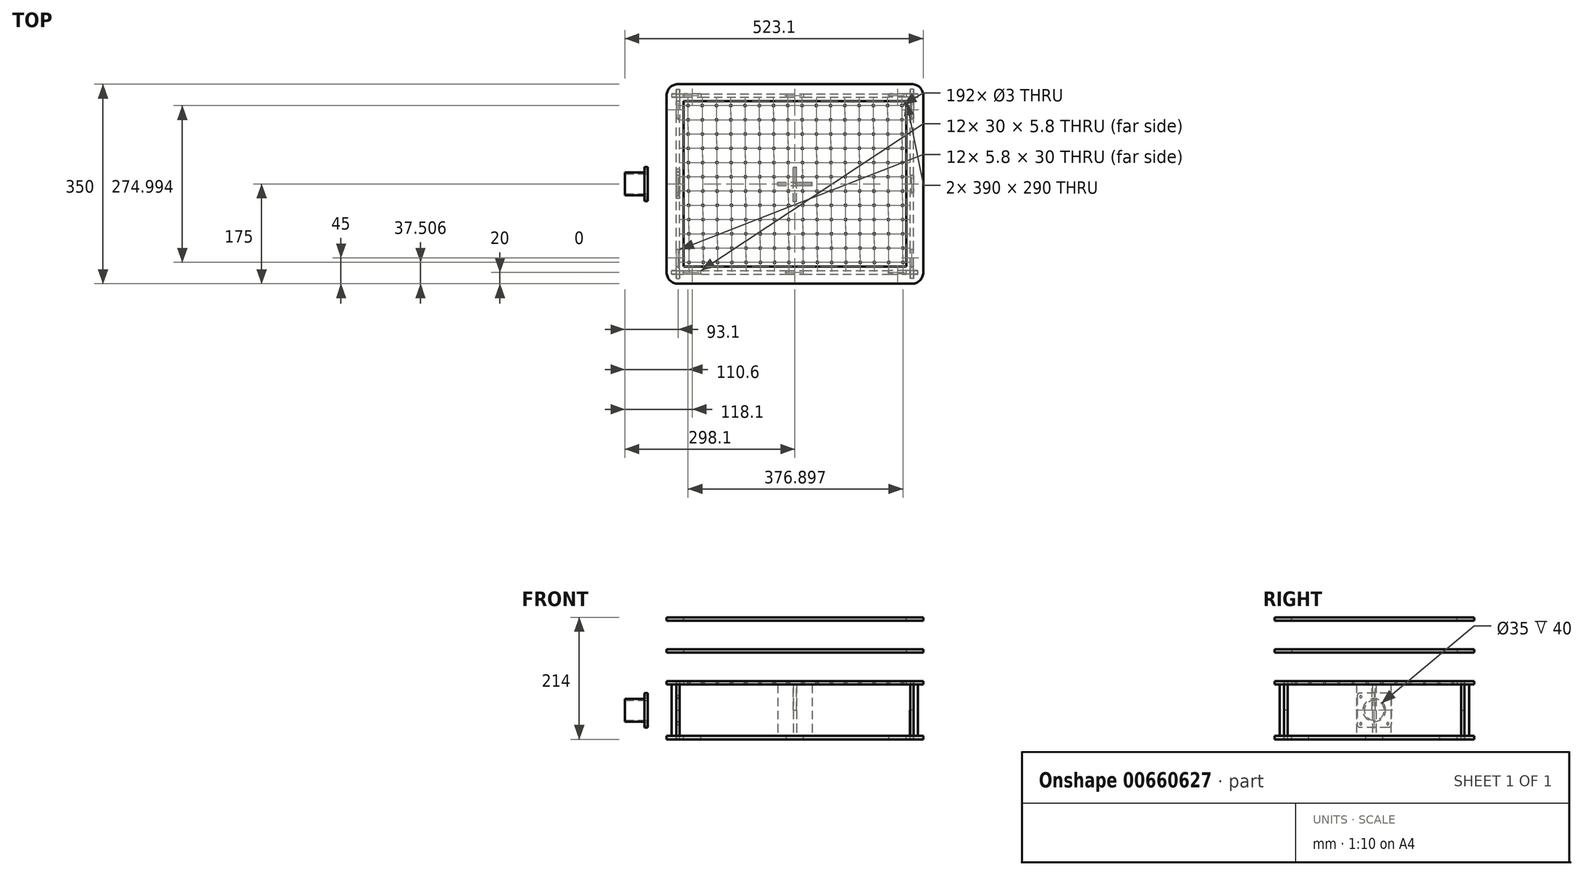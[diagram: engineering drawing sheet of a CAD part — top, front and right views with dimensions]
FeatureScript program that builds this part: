
annotation { "Feature Type Name" : "Feature", "Feature Type Description" : "" }
export const myFeature = defineFeature(function(context is Context, id is Id, definition is map)
    precondition{}
    {
        {
            var Q0;
            Q0=qCreatedBy(makeId("Top.planeOp"),FACE);
            var sketch = newSketch(context, id + "F0", { "sketchPlane" : qUnion([Q0])});
            skLineSegment(sketch, "E0.bottom", {"start": v(205, 175) * mm, "end": v(-205, 175) * mm});
            skLineSegment(sketch, "E0.top", {"start": v(205, -175) * mm, "end": v(-205, -175) * mm});
            skLineSegment(sketch, "E0.left", {"start": v(225, 155) * mm, "end": v(225, -155) * mm});
            skLineSegment(sketch, "E0.right", {"start": v(-225, 155) * mm, "end": v(-225, -155) * mm});
            skPoint(sketch, "E0.middle", {"position": v(0, 0) * mm});
            skPoint(sketch, "E1.visualSharp", {"position": v(-225, 175) * mm});
            skArc(sketch, "E1.filletArc", {"start": v(-205, 175) * mm, "mid": v(-219.14, 169.14) * mm, "end": v(-225, 155) * mm});
            skPoint(sketch, "E2.visualSharp", {"position": v(225, 175) * mm});
            skArc(sketch, "E2.filletArc", {"start": v(225, 155) * mm, "mid": v(219.14, 169.14) * mm, "end": v(205, 175) * mm});
            skPoint(sketch, "E3.visualSharp", {"position": v(225, -175) * mm});
            skArc(sketch, "E3.filletArc", {"start": v(205, -175) * mm, "mid": v(219.14, -169.14) * mm, "end": v(225, -155) * mm});
            skPoint(sketch, "E4.visualSharp", {"position": v(-225, -175) * mm});
            skArc(sketch, "E4.filletArc", {"start": v(-225, -155) * mm, "mid": v(-219.14, -169.14) * mm, "end": v(-205, -175) * mm});
            skLineSegment(sketch, "E5", {"start": v(205, -155) * mm, "end": v(205, 155) * mm, "construction": true});
            skLineSegment(sketch, "E6.bottom", {"start": v(-205, 155) * mm, "end": v(205, 155) * mm, "construction": true});
            skLineSegment(sketch, "E6.top", {"start": v(-205, -155) * mm, "end": v(205, -155) * mm, "construction": true});
            skLineSegment(sketch, "E6.left", {"start": v(-205, 155) * mm, "end": v(-205, -155) * mm, "construction": true});
            skCircle(sketch, "E7", {"center": v(-187.5, 137.5) * mm, "radius": 1.5 * mm});
            skCircle(sketch, "E8.1.0.0", {"center": v(-162.5, 137.5) * mm, "radius": 1.5 * mm});
            skCircle(sketch, "E8.2.0.0", {"center": v(-137.5, 137.5) * mm, "radius": 1.5 * mm});
            skCircle(sketch, "E8.3.0.0", {"center": v(-112.5, 137.5) * mm, "radius": 1.5 * mm});
            skCircle(sketch, "E8.4.0.0", {"center": v(-87.5, 137.5) * mm, "radius": 1.5 * mm});
            skCircle(sketch, "E8.5.0.0", {"center": v(-62.5, 137.5) * mm, "radius": 1.5 * mm});
            skCircle(sketch, "E8.6.0.0", {"center": v(-37.5, 137.5) * mm, "radius": 1.5 * mm});
            skCircle(sketch, "E8.7.0.0", {"center": v(-12.5, 137.5) * mm, "radius": 1.5 * mm});
            skCircle(sketch, "E8.8.0.0", {"center": v(12.5, 137.5) * mm, "radius": 1.5 * mm});
            skCircle(sketch, "E8.9.0.0", {"center": v(37.5, 137.5) * mm, "radius": 1.5 * mm});
            skCircle(sketch, "E8.10.0.0", {"center": v(62.5, 137.5) * mm, "radius": 1.5 * mm});
            skCircle(sketch, "E8.11.0.0", {"center": v(87.5, 137.5) * mm, "radius": 1.5 * mm});
            skCircle(sketch, "E8.12.0.0", {"center": v(112.5, 137.5) * mm, "radius": 1.5 * mm});
            skCircle(sketch, "E8.13.0.0", {"center": v(137.5, 137.5) * mm, "radius": 1.5 * mm});
            skCircle(sketch, "E8.14.0.0", {"center": v(162.5, 137.5) * mm, "radius": 1.5 * mm});
            skLineSegment(sketch, "E8.direction1", {"start": v(-187.5, 137.5) * mm, "end": v(-162.5, 137.5) * mm, "construction": true});
            skCircle(sketch, "E9.1.0.0", {"center": v(-187.33, 112.5) * mm, "radius": 1.5 * mm});
            skCircle(sketch, "E9.2.0.0", {"center": v(-187.16, 87.5) * mm, "radius": 1.5 * mm});
            skCircle(sketch, "E9.3.0.0", {"center": v(-186.98, 62.5) * mm, "radius": 1.5 * mm});
            skCircle(sketch, "E9.4.0.0", {"center": v(-186.81, 37.5) * mm, "radius": 1.5 * mm});
            skCircle(sketch, "E9.5.0.0", {"center": v(-186.64, 12.5) * mm, "radius": 1.5 * mm});
            skCircle(sketch, "E9.6.0.0", {"center": v(-186.47, -12.5) * mm, "radius": 1.5 * mm});
            skCircle(sketch, "E9.7.0.0", {"center": v(-186.3, -37.5) * mm, "radius": 1.5 * mm});
            skCircle(sketch, "E9.8.0.0", {"center": v(-186.12, -62.5) * mm, "radius": 1.5 * mm});
            skCircle(sketch, "E9.9.0.0", {"center": v(-185.95, -87.5) * mm, "radius": 1.5 * mm});
            skCircle(sketch, "E9.10.0.0", {"center": v(-185.78, -112.5) * mm, "radius": 1.5 * mm});
            skCircle(sketch, "E9.11.0.0", {"center": v(-185.6, -137.5) * mm, "radius": 1.5 * mm});
            skLineSegment(sketch, "E9.direction1", {"start": v(-187.5, 137.5) * mm, "end": v(-187.33, 112.5) * mm, "construction": true});
            skCircle(sketch, "E10.0.15.0", {"center": v(187.5, 137.5) * mm, "radius": 1.5 * mm});
            skCircle(sketch, "E11.1.0.0", {"center": v(-162.33, 112.5) * mm, "radius": 1.5 * mm});
            skCircle(sketch, "E11.1.0.1", {"center": v(-162.16, 87.5) * mm, "radius": 1.5 * mm});
            skCircle(sketch, "E11.1.0.2", {"center": v(-161.98, 62.5) * mm, "radius": 1.5 * mm});
            skCircle(sketch, "E11.1.0.3", {"center": v(-161.81, 37.5) * mm, "radius": 1.5 * mm});
            skCircle(sketch, "E11.1.0.4", {"center": v(-161.64, 12.5) * mm, "radius": 1.5 * mm});
            skCircle(sketch, "E11.1.0.5", {"center": v(-161.47, -12.5) * mm, "radius": 1.5 * mm});
            skCircle(sketch, "E11.1.0.6", {"center": v(-161.3, -37.5) * mm, "radius": 1.5 * mm});
            skCircle(sketch, "E11.1.0.7", {"center": v(-161.12, -62.5) * mm, "radius": 1.5 * mm});
            skCircle(sketch, "E11.1.0.8", {"center": v(-160.95, -87.5) * mm, "radius": 1.5 * mm});
            skCircle(sketch, "E11.1.0.9", {"center": v(-160.78, -112.5) * mm, "radius": 1.5 * mm});
            skCircle(sketch, "E11.1.0.10", {"center": v(-160.6, -137.5) * mm, "radius": 1.5 * mm});
            skCircle(sketch, "E11.2.0.0", {"center": v(-137.33, 112.5) * mm, "radius": 1.5 * mm});
            skCircle(sketch, "E11.2.0.1", {"center": v(-137.16, 87.5) * mm, "radius": 1.5 * mm});
            skCircle(sketch, "E11.2.0.2", {"center": v(-136.98, 62.5) * mm, "radius": 1.5 * mm});
            skCircle(sketch, "E11.2.0.3", {"center": v(-136.81, 37.5) * mm, "radius": 1.5 * mm});
            skCircle(sketch, "E11.2.0.4", {"center": v(-136.64, 12.5) * mm, "radius": 1.5 * mm});
            skCircle(sketch, "E11.2.0.5", {"center": v(-136.47, -12.5) * mm, "radius": 1.5 * mm});
            skCircle(sketch, "E11.2.0.6", {"center": v(-136.3, -37.5) * mm, "radius": 1.5 * mm});
            skCircle(sketch, "E11.2.0.7", {"center": v(-136.12, -62.5) * mm, "radius": 1.5 * mm});
            skCircle(sketch, "E11.2.0.8", {"center": v(-135.95, -87.5) * mm, "radius": 1.5 * mm});
            skCircle(sketch, "E11.2.0.9", {"center": v(-135.78, -112.5) * mm, "radius": 1.5 * mm});
            skCircle(sketch, "E11.2.0.10", {"center": v(-135.6, -137.5) * mm, "radius": 1.5 * mm});
            skCircle(sketch, "E11.3.0.0", {"center": v(-112.33, 112.5) * mm, "radius": 1.5 * mm});
            skCircle(sketch, "E11.3.0.1", {"center": v(-112.16, 87.5) * mm, "radius": 1.5 * mm});
            skCircle(sketch, "E11.3.0.2", {"center": v(-111.98, 62.5) * mm, "radius": 1.5 * mm});
            skCircle(sketch, "E11.3.0.3", {"center": v(-111.81, 37.5) * mm, "radius": 1.5 * mm});
            skCircle(sketch, "E11.3.0.4", {"center": v(-111.64, 12.5) * mm, "radius": 1.5 * mm});
            skCircle(sketch, "E11.3.0.5", {"center": v(-111.47, -12.5) * mm, "radius": 1.5 * mm});
            skCircle(sketch, "E11.3.0.6", {"center": v(-111.3, -37.5) * mm, "radius": 1.5 * mm});
            skCircle(sketch, "E11.3.0.7", {"center": v(-111.12, -62.5) * mm, "radius": 1.5 * mm});
            skCircle(sketch, "E11.3.0.8", {"center": v(-110.95, -87.5) * mm, "radius": 1.5 * mm});
            skCircle(sketch, "E11.3.0.9", {"center": v(-110.78, -112.5) * mm, "radius": 1.5 * mm});
            skCircle(sketch, "E11.3.0.10", {"center": v(-110.6, -137.5) * mm, "radius": 1.5 * mm});
            skCircle(sketch, "E11.4.0.0", {"center": v(-87.33, 112.5) * mm, "radius": 1.5 * mm});
            skCircle(sketch, "E11.4.0.1", {"center": v(-87.16, 87.5) * mm, "radius": 1.5 * mm});
            skCircle(sketch, "E11.4.0.2", {"center": v(-86.98, 62.5) * mm, "radius": 1.5 * mm});
            skCircle(sketch, "E11.4.0.3", {"center": v(-86.81, 37.5) * mm, "radius": 1.5 * mm});
            skCircle(sketch, "E11.4.0.4", {"center": v(-86.64, 12.5) * mm, "radius": 1.5 * mm});
            skCircle(sketch, "E11.4.0.5", {"center": v(-86.47, -12.5) * mm, "radius": 1.5 * mm});
            skCircle(sketch, "E11.4.0.6", {"center": v(-86.3, -37.5) * mm, "radius": 1.5 * mm});
            skCircle(sketch, "E11.4.0.7", {"center": v(-86.12, -62.5) * mm, "radius": 1.5 * mm});
            skCircle(sketch, "E11.4.0.8", {"center": v(-85.95, -87.5) * mm, "radius": 1.5 * mm});
            skCircle(sketch, "E11.4.0.9", {"center": v(-85.78, -112.5) * mm, "radius": 1.5 * mm});
            skCircle(sketch, "E11.4.0.10", {"center": v(-85.6, -137.5) * mm, "radius": 1.5 * mm});
            skCircle(sketch, "E11.5.0.0", {"center": v(-62.33, 112.5) * mm, "radius": 1.5 * mm});
            skCircle(sketch, "E11.5.0.1", {"center": v(-62.16, 87.5) * mm, "radius": 1.5 * mm});
            skCircle(sketch, "E11.5.0.2", {"center": v(-61.98, 62.5) * mm, "radius": 1.5 * mm});
            skCircle(sketch, "E11.5.0.3", {"center": v(-61.81, 37.5) * mm, "radius": 1.5 * mm});
            skCircle(sketch, "E11.5.0.4", {"center": v(-61.64, 12.5) * mm, "radius": 1.5 * mm});
            skCircle(sketch, "E11.5.0.5", {"center": v(-61.47, -12.5) * mm, "radius": 1.5 * mm});
            skCircle(sketch, "E11.5.0.6", {"center": v(-61.3, -37.5) * mm, "radius": 1.5 * mm});
            skCircle(sketch, "E11.5.0.7", {"center": v(-61.12, -62.5) * mm, "radius": 1.5 * mm});
            skCircle(sketch, "E11.5.0.8", {"center": v(-60.95, -87.5) * mm, "radius": 1.5 * mm});
            skCircle(sketch, "E11.5.0.9", {"center": v(-60.78, -112.5) * mm, "radius": 1.5 * mm});
            skCircle(sketch, "E11.5.0.10", {"center": v(-60.6, -137.5) * mm, "radius": 1.5 * mm});
            skCircle(sketch, "E11.6.0.0", {"center": v(-37.33, 112.5) * mm, "radius": 1.5 * mm});
            skCircle(sketch, "E11.6.0.1", {"center": v(-37.16, 87.5) * mm, "radius": 1.5 * mm});
            skCircle(sketch, "E11.6.0.2", {"center": v(-36.98, 62.5) * mm, "radius": 1.5 * mm});
            skCircle(sketch, "E11.6.0.3", {"center": v(-36.81, 37.5) * mm, "radius": 1.5 * mm});
            skCircle(sketch, "E11.6.0.4", {"center": v(-36.64, 12.5) * mm, "radius": 1.5 * mm});
            skCircle(sketch, "E11.6.0.5", {"center": v(-36.47, -12.5) * mm, "radius": 1.5 * mm});
            skCircle(sketch, "E11.6.0.6", {"center": v(-36.3, -37.5) * mm, "radius": 1.5 * mm});
            skCircle(sketch, "E11.6.0.7", {"center": v(-36.12, -62.5) * mm, "radius": 1.5 * mm});
            skCircle(sketch, "E11.6.0.8", {"center": v(-35.95, -87.5) * mm, "radius": 1.5 * mm});
            skCircle(sketch, "E11.6.0.9", {"center": v(-35.78, -112.5) * mm, "radius": 1.5 * mm});
            skCircle(sketch, "E11.6.0.10", {"center": v(-35.6, -137.5) * mm, "radius": 1.5 * mm});
            skCircle(sketch, "E11.7.0.0", {"center": v(-12.33, 112.5) * mm, "radius": 1.5 * mm});
            skCircle(sketch, "E11.7.0.1", {"center": v(-12.16, 87.5) * mm, "radius": 1.5 * mm});
            skCircle(sketch, "E11.7.0.2", {"center": v(-11.98, 62.5) * mm, "radius": 1.5 * mm});
            skCircle(sketch, "E11.7.0.3", {"center": v(-11.81, 37.5) * mm, "radius": 1.5 * mm});
            skCircle(sketch, "E11.7.0.4", {"center": v(-11.64, 12.5) * mm, "radius": 1.5 * mm});
            skCircle(sketch, "E11.7.0.5", {"center": v(-11.47, -12.5) * mm, "radius": 1.5 * mm});
            skCircle(sketch, "E11.7.0.6", {"center": v(-11.3, -37.5) * mm, "radius": 1.5 * mm});
            skCircle(sketch, "E11.7.0.7", {"center": v(-11.12, -62.5) * mm, "radius": 1.5 * mm});
            skCircle(sketch, "E11.7.0.8", {"center": v(-10.95, -87.5) * mm, "radius": 1.5 * mm});
            skCircle(sketch, "E11.7.0.9", {"center": v(-10.78, -112.5) * mm, "radius": 1.5 * mm});
            skCircle(sketch, "E11.7.0.10", {"center": v(-10.6, -137.5) * mm, "radius": 1.5 * mm});
            skCircle(sketch, "E11.8.0.0", {"center": v(12.67, 112.5) * mm, "radius": 1.5 * mm});
            skCircle(sketch, "E11.8.0.1", {"center": v(12.84, 87.5) * mm, "radius": 1.5 * mm});
            skCircle(sketch, "E11.8.0.2", {"center": v(13.02, 62.5) * mm, "radius": 1.5 * mm});
            skCircle(sketch, "E11.8.0.3", {"center": v(13.19, 37.5) * mm, "radius": 1.5 * mm});
            skCircle(sketch, "E11.8.0.4", {"center": v(13.36, 12.5) * mm, "radius": 1.5 * mm});
            skCircle(sketch, "E11.8.0.5", {"center": v(13.53, -12.5) * mm, "radius": 1.5 * mm});
            skCircle(sketch, "E11.8.0.6", {"center": v(13.7, -37.5) * mm, "radius": 1.5 * mm});
            skCircle(sketch, "E11.8.0.7", {"center": v(13.88, -62.5) * mm, "radius": 1.5 * mm});
            skCircle(sketch, "E11.8.0.8", {"center": v(14.05, -87.5) * mm, "radius": 1.5 * mm});
            skCircle(sketch, "E11.8.0.9", {"center": v(14.22, -112.5) * mm, "radius": 1.5 * mm});
            skCircle(sketch, "E11.8.0.10", {"center": v(14.4, -137.5) * mm, "radius": 1.5 * mm});
            skCircle(sketch, "E11.9.0.0", {"center": v(37.67, 112.5) * mm, "radius": 1.5 * mm});
            skCircle(sketch, "E11.9.0.1", {"center": v(37.84, 87.5) * mm, "radius": 1.5 * mm});
            skCircle(sketch, "E11.9.0.2", {"center": v(38.02, 62.5) * mm, "radius": 1.5 * mm});
            skCircle(sketch, "E11.9.0.3", {"center": v(38.19, 37.5) * mm, "radius": 1.5 * mm});
            skCircle(sketch, "E11.9.0.4", {"center": v(38.36, 12.5) * mm, "radius": 1.5 * mm});
            skCircle(sketch, "E11.9.0.5", {"center": v(38.53, -12.5) * mm, "radius": 1.5 * mm});
            skCircle(sketch, "E11.9.0.6", {"center": v(38.7, -37.5) * mm, "radius": 1.5 * mm});
            skCircle(sketch, "E11.9.0.7", {"center": v(38.88, -62.5) * mm, "radius": 1.5 * mm});
            skCircle(sketch, "E11.9.0.8", {"center": v(39.05, -87.5) * mm, "radius": 1.5 * mm});
            skCircle(sketch, "E11.9.0.9", {"center": v(39.22, -112.5) * mm, "radius": 1.5 * mm});
            skCircle(sketch, "E11.9.0.10", {"center": v(39.4, -137.5) * mm, "radius": 1.5 * mm});
            skCircle(sketch, "E11.10.0.0", {"center": v(62.67, 112.5) * mm, "radius": 1.5 * mm});
            skCircle(sketch, "E11.10.0.1", {"center": v(62.84, 87.5) * mm, "radius": 1.5 * mm});
            skCircle(sketch, "E11.10.0.2", {"center": v(63.02, 62.5) * mm, "radius": 1.5 * mm});
            skCircle(sketch, "E11.10.0.3", {"center": v(63.19, 37.5) * mm, "radius": 1.5 * mm});
            skCircle(sketch, "E11.10.0.4", {"center": v(63.36, 12.5) * mm, "radius": 1.5 * mm});
            skCircle(sketch, "E11.10.0.5", {"center": v(63.53, -12.5) * mm, "radius": 1.5 * mm});
            skCircle(sketch, "E11.10.0.6", {"center": v(63.7, -37.5) * mm, "radius": 1.5 * mm});
            skCircle(sketch, "E11.10.0.7", {"center": v(63.88, -62.5) * mm, "radius": 1.5 * mm});
            skCircle(sketch, "E11.10.0.8", {"center": v(64.05, -87.5) * mm, "radius": 1.5 * mm});
            skCircle(sketch, "E11.10.0.9", {"center": v(64.22, -112.5) * mm, "radius": 1.5 * mm});
            skCircle(sketch, "E11.10.0.10", {"center": v(64.4, -137.5) * mm, "radius": 1.5 * mm});
            skCircle(sketch, "E11.11.0.0", {"center": v(87.67, 112.5) * mm, "radius": 1.5 * mm});
            skCircle(sketch, "E11.11.0.1", {"center": v(87.84, 87.5) * mm, "radius": 1.5 * mm});
            skCircle(sketch, "E11.11.0.2", {"center": v(88.02, 62.5) * mm, "radius": 1.5 * mm});
            skCircle(sketch, "E11.11.0.3", {"center": v(88.19, 37.5) * mm, "radius": 1.5 * mm});
            skCircle(sketch, "E11.11.0.4", {"center": v(88.36, 12.5) * mm, "radius": 1.5 * mm});
            skCircle(sketch, "E11.11.0.5", {"center": v(88.53, -12.5) * mm, "radius": 1.5 * mm});
            skCircle(sketch, "E11.11.0.6", {"center": v(88.7, -37.5) * mm, "radius": 1.5 * mm});
            skCircle(sketch, "E11.11.0.7", {"center": v(88.88, -62.5) * mm, "radius": 1.5 * mm});
            skCircle(sketch, "E11.11.0.8", {"center": v(89.05, -87.5) * mm, "radius": 1.5 * mm});
            skCircle(sketch, "E11.11.0.9", {"center": v(89.22, -112.5) * mm, "radius": 1.5 * mm});
            skCircle(sketch, "E11.11.0.10", {"center": v(89.4, -137.5) * mm, "radius": 1.5 * mm});
            skCircle(sketch, "E11.12.0.0", {"center": v(112.67, 112.5) * mm, "radius": 1.5 * mm});
            skCircle(sketch, "E11.12.0.1", {"center": v(112.84, 87.5) * mm, "radius": 1.5 * mm});
            skCircle(sketch, "E11.12.0.2", {"center": v(113.02, 62.5) * mm, "radius": 1.5 * mm});
            skCircle(sketch, "E11.12.0.3", {"center": v(113.19, 37.5) * mm, "radius": 1.5 * mm});
            skCircle(sketch, "E11.12.0.4", {"center": v(113.36, 12.5) * mm, "radius": 1.5 * mm});
            skCircle(sketch, "E11.12.0.5", {"center": v(113.53, -12.5) * mm, "radius": 1.5 * mm});
            skCircle(sketch, "E11.12.0.6", {"center": v(113.7, -37.5) * mm, "radius": 1.5 * mm});
            skCircle(sketch, "E11.12.0.7", {"center": v(113.88, -62.5) * mm, "radius": 1.5 * mm});
            skCircle(sketch, "E11.12.0.8", {"center": v(114.05, -87.5) * mm, "radius": 1.5 * mm});
            skCircle(sketch, "E11.12.0.9", {"center": v(114.22, -112.5) * mm, "radius": 1.5 * mm});
            skCircle(sketch, "E11.12.0.10", {"center": v(114.4, -137.5) * mm, "radius": 1.5 * mm});
            skCircle(sketch, "E11.13.0.0", {"center": v(137.67, 112.5) * mm, "radius": 1.5 * mm});
            skCircle(sketch, "E11.13.0.1", {"center": v(137.84, 87.5) * mm, "radius": 1.5 * mm});
            skCircle(sketch, "E11.13.0.2", {"center": v(138.02, 62.5) * mm, "radius": 1.5 * mm});
            skCircle(sketch, "E11.13.0.3", {"center": v(138.19, 37.5) * mm, "radius": 1.5 * mm});
            skCircle(sketch, "E11.13.0.4", {"center": v(138.36, 12.5) * mm, "radius": 1.5 * mm});
            skCircle(sketch, "E11.13.0.5", {"center": v(138.53, -12.5) * mm, "radius": 1.5 * mm});
            skCircle(sketch, "E11.13.0.6", {"center": v(138.7, -37.5) * mm, "radius": 1.5 * mm});
            skCircle(sketch, "E11.13.0.7", {"center": v(138.88, -62.5) * mm, "radius": 1.5 * mm});
            skCircle(sketch, "E11.13.0.8", {"center": v(139.05, -87.5) * mm, "radius": 1.5 * mm});
            skCircle(sketch, "E11.13.0.9", {"center": v(139.22, -112.5) * mm, "radius": 1.5 * mm});
            skCircle(sketch, "E11.13.0.10", {"center": v(139.4, -137.5) * mm, "radius": 1.5 * mm});
            skCircle(sketch, "E11.14.0.0", {"center": v(162.67, 112.5) * mm, "radius": 1.5 * mm});
            skCircle(sketch, "E11.14.0.1", {"center": v(162.84, 87.5) * mm, "radius": 1.5 * mm});
            skCircle(sketch, "E11.14.0.2", {"center": v(163.02, 62.5) * mm, "radius": 1.5 * mm});
            skCircle(sketch, "E11.14.0.3", {"center": v(163.19, 37.5) * mm, "radius": 1.5 * mm});
            skCircle(sketch, "E11.14.0.4", {"center": v(163.36, 12.5) * mm, "radius": 1.5 * mm});
            skCircle(sketch, "E11.14.0.5", {"center": v(163.53, -12.5) * mm, "radius": 1.5 * mm});
            skCircle(sketch, "E11.14.0.6", {"center": v(163.7, -37.5) * mm, "radius": 1.5 * mm});
            skCircle(sketch, "E11.14.0.7", {"center": v(163.88, -62.5) * mm, "radius": 1.5 * mm});
            skCircle(sketch, "E11.14.0.8", {"center": v(164.05, -87.5) * mm, "radius": 1.5 * mm});
            skCircle(sketch, "E11.14.0.9", {"center": v(164.22, -112.5) * mm, "radius": 1.5 * mm});
            skCircle(sketch, "E11.14.0.10", {"center": v(164.4, -137.5) * mm, "radius": 1.5 * mm});
            skCircle(sketch, "E11.15.0.0", {"center": v(187.67, 112.5) * mm, "radius": 1.5 * mm});
            skCircle(sketch, "E11.15.0.1", {"center": v(187.84, 87.5) * mm, "radius": 1.5 * mm});
            skCircle(sketch, "E11.15.0.2", {"center": v(188.02, 62.5) * mm, "radius": 1.5 * mm});
            skCircle(sketch, "E11.15.0.3", {"center": v(188.19, 37.5) * mm, "radius": 1.5 * mm});
            skCircle(sketch, "E11.15.0.4", {"center": v(188.36, 12.5) * mm, "radius": 1.5 * mm});
            skCircle(sketch, "E11.15.0.5", {"center": v(188.53, -12.5) * mm, "radius": 1.5 * mm});
            skCircle(sketch, "E11.15.0.6", {"center": v(188.7, -37.5) * mm, "radius": 1.5 * mm});
            skCircle(sketch, "E11.15.0.7", {"center": v(188.88, -62.5) * mm, "radius": 1.5 * mm});
            skCircle(sketch, "E11.15.0.8", {"center": v(189.05, -87.5) * mm, "radius": 1.5 * mm});
            skCircle(sketch, "E11.15.0.9", {"center": v(189.22, -112.5) * mm, "radius": 1.5 * mm});
            skCircle(sketch, "E11.15.0.10", {"center": v(189.4, -137.5) * mm, "radius": 1.5 * mm});
            skLineSegment(sketch, "E11.direction1", {"start": v(-187.33, 112.5) * mm, "end": v(-162.33, 112.5) * mm, "construction": true});
            skLineSegment(sketch, "E12", {"start": v(0, 0) * mm, "end": v(0, 209.09) * mm, "construction": true});
            skPoint(sketch, "E12.endSnap0", {"position": v(0, 175) * mm});
            skLineSegment(sketch, "E13", {"start": v(0, 209.09) * mm, "end": v(0, 128.36) * mm, "construction": true});
            skLineSegment(sketch, "E14", {"start": v(0, 0) * mm, "end": v(-306.75, 0) * mm, "construction": true});
            skLineSegment(sketch, "E15.bottom", {"start": v(-195, 157.9) * mm, "end": v(-165, 157.9) * mm});
            skLineSegment(sketch, "E15.top", {"start": v(-195, 152.1) * mm, "end": v(-165, 152.1) * mm});
            skLineSegment(sketch, "E15.left", {"start": v(-195, 157.9) * mm, "end": v(-195, 152.1) * mm});
            skLineSegment(sketch, "E15.right", {"start": v(-165, 157.9) * mm, "end": v(-165, 152.1) * mm});
            skLineSegment(sketch, "E16.bottom", {"start": v(-15, 157.9) * mm, "end": v(15, 157.9) * mm});
            skLineSegment(sketch, "E16.top", {"start": v(-15, 152.1) * mm, "end": v(15, 152.1) * mm});
            skLineSegment(sketch, "E16.left", {"start": v(-15, 157.9) * mm, "end": v(-15, 152.1) * mm});
            skLineSegment(sketch, "E16.right", {"start": v(15, 157.9) * mm, "end": v(15, 152.1) * mm});
            skLineSegment(sketch, "E17.MirrorCS", {"start": v(195, 157.9) * mm, "end": v(195, 152.1) * mm});
            skLineSegment(sketch, "E18.MirrorCS", {"start": v(195, 157.9) * mm, "end": v(165, 157.9) * mm});
            skLineSegment(sketch, "E19.MirrorCS", {"start": v(195, 152.1) * mm, "end": v(165, 152.1) * mm});
            skLineSegment(sketch, "E20.MirrorCS", {"start": v(165, 157.9) * mm, "end": v(165, 152.1) * mm});
            skLineSegment(sketch, "E21.MirrorCS", {"start": v(165, -157.9) * mm, "end": v(165, -152.1) * mm});
            skLineSegment(sketch, "E22.MirrorCS", {"start": v(195, -157.9) * mm, "end": v(165, -157.9) * mm});
            skLineSegment(sketch, "E23.MirrorCS", {"start": v(195, -157.9) * mm, "end": v(195, -152.1) * mm});
            skLineSegment(sketch, "E24.MirrorCS", {"start": v(195, -152.1) * mm, "end": v(165, -152.1) * mm});
            skLineSegment(sketch, "E25.MirrorCS", {"start": v(15, -157.9) * mm, "end": v(15, -152.1) * mm});
            skLineSegment(sketch, "E26.MirrorCS", {"start": v(-15, -157.9) * mm, "end": v(15, -157.9) * mm});
            skLineSegment(sketch, "E27.MirrorCS", {"start": v(-15, -157.9) * mm, "end": v(-15, -152.1) * mm});
            skLineSegment(sketch, "E28.MirrorCS", {"start": v(-15, -152.1) * mm, "end": v(15, -152.1) * mm});
            skLineSegment(sketch, "E29.MirrorCS", {"start": v(-165, -157.9) * mm, "end": v(-165, -152.1) * mm});
            skLineSegment(sketch, "E30.MirrorCS", {"start": v(-195, -157.9) * mm, "end": v(-165, -157.9) * mm});
            skLineSegment(sketch, "E31.MirrorCS", {"start": v(-195, -157.9) * mm, "end": v(-195, -152.1) * mm});
            skLineSegment(sketch, "E32.MirrorCS", {"start": v(-195, -152.1) * mm, "end": v(-165, -152.1) * mm});
            skLineSegment(sketch, "E33.bottom", {"start": v(-202.1, 145) * mm, "end": v(-202.1, 115) * mm});
            skLineSegment(sketch, "E33.top", {"start": v(-207.9, 145) * mm, "end": v(-207.9, 115) * mm});
            skLineSegment(sketch, "E33.left", {"start": v(-202.1, 145) * mm, "end": v(-207.9, 145) * mm});
            skLineSegment(sketch, "E33.right", {"start": v(-202.1, 115) * mm, "end": v(-207.9, 115) * mm});
            skLineSegment(sketch, "E34.bottom", {"start": v(-202.1, 15) * mm, "end": v(-202.1, -15) * mm});
            skLineSegment(sketch, "E34.top", {"start": v(-207.9, 15) * mm, "end": v(-207.9, -15) * mm});
            skLineSegment(sketch, "E34.left", {"start": v(-202.1, 15) * mm, "end": v(-207.9, 15) * mm});
            skLineSegment(sketch, "E34.right", {"start": v(-202.1, -15) * mm, "end": v(-207.9, -15) * mm});
            skLineSegment(sketch, "E35.MirrorCS", {"start": v(-202.1, -115) * mm, "end": v(-207.9, -115) * mm});
            skLineSegment(sketch, "E36.MirrorCS", {"start": v(-202.1, -145) * mm, "end": v(-207.9, -145) * mm});
            skLineSegment(sketch, "E37.MirrorCS", {"start": v(-202.1, -145) * mm, "end": v(-202.1, -115) * mm});
            skLineSegment(sketch, "E38.MirrorCS", {"start": v(-207.9, -145) * mm, "end": v(-207.9, -115) * mm});
            skLineSegment(sketch, "E39.MirrorCS", {"start": v(202.1, 145) * mm, "end": v(207.9, 145) * mm});
            skLineSegment(sketch, "E40.MirrorCS", {"start": v(202.1, 145) * mm, "end": v(202.1, 115) * mm});
            skLineSegment(sketch, "E41.MirrorCS", {"start": v(207.9, 145) * mm, "end": v(207.9, 115) * mm});
            skLineSegment(sketch, "E42.MirrorCS", {"start": v(202.1, 115) * mm, "end": v(207.9, 115) * mm});
            skLineSegment(sketch, "E43.MirrorCS", {"start": v(202.1, 15) * mm, "end": v(207.9, 15) * mm});
            skLineSegment(sketch, "E44.MirrorCS", {"start": v(207.9, 15) * mm, "end": v(207.9, -15) * mm});
            skLineSegment(sketch, "E45.MirrorCS", {"start": v(202.1, 15) * mm, "end": v(202.1, -15) * mm});
            skLineSegment(sketch, "E46.MirrorCS", {"start": v(202.1, -15) * mm, "end": v(207.9, -15) * mm});
            skLineSegment(sketch, "E47.MirrorCS", {"start": v(202.1, -115) * mm, "end": v(207.9, -115) * mm});
            skLineSegment(sketch, "E48.MirrorCS", {"start": v(202.1, -145) * mm, "end": v(207.9, -145) * mm});
            skLineSegment(sketch, "E49.MirrorCS", {"start": v(202.1, -145) * mm, "end": v(202.1, -115) * mm});
            skLineSegment(sketch, "E50.MirrorCS", {"start": v(207.9, -145) * mm, "end": v(207.9, -115) * mm});
            skSolve(sketch);
        }
        {
            var Q0;
            Q0 = qSketchRegion(id + "F0", true);
            extrude(context, id + "F1", {"entities" : qUnion([Q0]), "depth" : 6 * mm, "offsetDistance" : 25 * mm});
        }
        {
            var Q0;
            Q0=qCreatedBy(makeId("Top.planeOp"),FACE);
            cPlane(context, id + "F2", {"entities" : qUnion([Q0]), "cplaneType" : CPlaneType.OFFSET, "offset" : 90 * mm, "oppositeDirection" : true, "width" : 150 * mm, "height" : 150 * mm});
        }
        {
            var Q0;
            Q0=qCreatedBy(id+"F2.planeOp",FACE);
            var sketch = newSketch(context, id + "F3", { "sketchPlane" : qUnion([Q0])});
            skLineSegment(sketch, "E51.bottom", {"start": v(205, 175) * mm, "end": v(-205, 175) * mm});
            skLineSegment(sketch, "E51.top", {"start": v(205, -175) * mm, "end": v(-205, -175) * mm});
            skLineSegment(sketch, "E51.left", {"start": v(225, 155) * mm, "end": v(225, -155) * mm});
            skLineSegment(sketch, "E51.right", {"start": v(-225, 155) * mm, "end": v(-225, -155) * mm});
            skPoint(sketch, "E52.visualSharp", {"position": v(-225, 175) * mm});
            skArc(sketch, "E52.filletArc", {"start": v(-205, 175) * mm, "mid": v(-219.14, 169.14) * mm, "end": v(-225, 155) * mm});
            skPoint(sketch, "E53.visualSharp", {"position": v(225, 175) * mm});
            skArc(sketch, "E53.filletArc", {"start": v(225, 155) * mm, "mid": v(219.14, 169.14) * mm, "end": v(205, 175) * mm});
            skPoint(sketch, "E54.visualSharp", {"position": v(225, -175) * mm});
            skArc(sketch, "E54.filletArc", {"start": v(205, -175) * mm, "mid": v(219.14, -169.14) * mm, "end": v(225, -155) * mm});
            skPoint(sketch, "E55.visualSharp", {"position": v(-225, -175) * mm});
            skArc(sketch, "E55.filletArc", {"start": v(-225, -155) * mm, "mid": v(-219.14, -169.14) * mm, "end": v(-205, -175) * mm});
            skPoint(sketch, "E56.endSnap0", {"position": v(0, 175) * mm});
            skLineSegment(sketch, "E57.bottom", {"start": v(-195, 157.9) * mm, "end": v(-165, 157.9) * mm});
            skLineSegment(sketch, "E57.top", {"start": v(-195, 152.1) * mm, "end": v(-165, 152.1) * mm});
            skLineSegment(sketch, "E57.left", {"start": v(-195, 157.9) * mm, "end": v(-195, 152.1) * mm});
            skLineSegment(sketch, "E57.right", {"start": v(-165, 157.9) * mm, "end": v(-165, 152.1) * mm});
            skLineSegment(sketch, "E58.bottom", {"start": v(-15, 157.9) * mm, "end": v(15, 157.9) * mm});
            skLineSegment(sketch, "E58.top", {"start": v(-15, 152.1) * mm, "end": v(15, 152.1) * mm});
            skLineSegment(sketch, "E58.left", {"start": v(-15, 157.9) * mm, "end": v(-15, 152.1) * mm});
            skLineSegment(sketch, "E58.right", {"start": v(15, 157.9) * mm, "end": v(15, 152.1) * mm});
            skLineSegment(sketch, "E59.MirrorCS", {"start": v(195, 157.9) * mm, "end": v(195, 152.1) * mm});
            skLineSegment(sketch, "E60.MirrorCS", {"start": v(195, 157.9) * mm, "end": v(165, 157.9) * mm});
            skLineSegment(sketch, "E61.MirrorCS", {"start": v(195, 152.1) * mm, "end": v(165, 152.1) * mm});
            skLineSegment(sketch, "E62.MirrorCS", {"start": v(165, 157.9) * mm, "end": v(165, 152.1) * mm});
            skLineSegment(sketch, "E63.MirrorCS", {"start": v(165, -157.9) * mm, "end": v(165, -152.1) * mm});
            skLineSegment(sketch, "E64.MirrorCS", {"start": v(195, -157.9) * mm, "end": v(165, -157.9) * mm});
            skLineSegment(sketch, "E65.MirrorCS", {"start": v(195, -157.9) * mm, "end": v(195, -152.1) * mm});
            skLineSegment(sketch, "E66.MirrorCS", {"start": v(195, -152.1) * mm, "end": v(165, -152.1) * mm});
            skLineSegment(sketch, "E67.MirrorCS", {"start": v(15, -157.9) * mm, "end": v(15, -152.1) * mm});
            skLineSegment(sketch, "E68.MirrorCS", {"start": v(-15, -157.9) * mm, "end": v(15, -157.9) * mm});
            skLineSegment(sketch, "E69.MirrorCS", {"start": v(-15, -157.9) * mm, "end": v(-15, -152.1) * mm});
            skLineSegment(sketch, "E70.MirrorCS", {"start": v(-15, -152.1) * mm, "end": v(15, -152.1) * mm});
            skLineSegment(sketch, "E71.MirrorCS", {"start": v(-165, -157.9) * mm, "end": v(-165, -152.1) * mm});
            skLineSegment(sketch, "E72.MirrorCS", {"start": v(-195, -157.9) * mm, "end": v(-165, -157.9) * mm});
            skLineSegment(sketch, "E73.MirrorCS", {"start": v(-195, -157.9) * mm, "end": v(-195, -152.1) * mm});
            skLineSegment(sketch, "E74.MirrorCS", {"start": v(-195, -152.1) * mm, "end": v(-165, -152.1) * mm});
            skLineSegment(sketch, "E75.bottom", {"start": v(-202.1, 145) * mm, "end": v(-202.1, 115) * mm});
            skLineSegment(sketch, "E75.top", {"start": v(-207.9, 145) * mm, "end": v(-207.9, 115) * mm});
            skLineSegment(sketch, "E75.left", {"start": v(-202.1, 145) * mm, "end": v(-207.9, 145) * mm});
            skLineSegment(sketch, "E75.right", {"start": v(-202.1, 115) * mm, "end": v(-207.9, 115) * mm});
            skLineSegment(sketch, "E76.bottom", {"start": v(-202.1, 15) * mm, "end": v(-202.1, -15) * mm});
            skLineSegment(sketch, "E76.top", {"start": v(-207.9, 15) * mm, "end": v(-207.9, -15) * mm});
            skLineSegment(sketch, "E76.left", {"start": v(-202.1, 15) * mm, "end": v(-207.9, 15) * mm});
            skLineSegment(sketch, "E76.right", {"start": v(-202.1, -15) * mm, "end": v(-207.9, -15) * mm});
            skLineSegment(sketch, "E77.MirrorCS", {"start": v(-202.1, -115) * mm, "end": v(-207.9, -115) * mm});
            skLineSegment(sketch, "E78.MirrorCS", {"start": v(-202.1, -145) * mm, "end": v(-207.9, -145) * mm});
            skLineSegment(sketch, "E79.MirrorCS", {"start": v(-202.1, -145) * mm, "end": v(-202.1, -115) * mm});
            skLineSegment(sketch, "E80.MirrorCS", {"start": v(-207.9, -145) * mm, "end": v(-207.9, -115) * mm});
            skLineSegment(sketch, "E81.MirrorCS", {"start": v(202.1, 145) * mm, "end": v(207.9, 145) * mm});
            skLineSegment(sketch, "E82.MirrorCS", {"start": v(202.1, 145) * mm, "end": v(202.1, 115) * mm});
            skLineSegment(sketch, "E83.MirrorCS", {"start": v(207.9, 145) * mm, "end": v(207.9, 115) * mm});
            skLineSegment(sketch, "E84.MirrorCS", {"start": v(202.1, 115) * mm, "end": v(207.9, 115) * mm});
            skLineSegment(sketch, "E85.MirrorCS", {"start": v(202.1, 15) * mm, "end": v(207.9, 15) * mm});
            skLineSegment(sketch, "E86.MirrorCS", {"start": v(207.9, 15) * mm, "end": v(207.9, -15) * mm});
            skLineSegment(sketch, "E87.MirrorCS", {"start": v(202.1, 15) * mm, "end": v(202.1, -15) * mm});
            skLineSegment(sketch, "E88.MirrorCS", {"start": v(202.1, -15) * mm, "end": v(207.9, -15) * mm});
            skLineSegment(sketch, "E89", {"start": v(0, 0) * mm, "end": v(0, -76.94) * mm, "construction": true});
            skLineSegment(sketch, "E90.MirrorCS", {"start": v(202.1, -145) * mm, "end": v(207.9, -145) * mm});
            skLineSegment(sketch, "E91.MirrorCS", {"start": v(202.1, -115) * mm, "end": v(207.9, -115) * mm});
            skLineSegment(sketch, "E92.MirrorCS", {"start": v(202.1, -145) * mm, "end": v(202.1, -115) * mm});
            skLineSegment(sketch, "E93.MirrorCS", {"start": v(207.9, -145) * mm, "end": v(207.9, -115) * mm});
            skSolve(sketch);
        }
        {
            var Q0;
            Q0 = qSketchRegion(id + "F3", true);
            extrude(context, id + "F4", {"entities" : qUnion([Q0]), "oppositeDirection" : true, "depth" : 6 * mm, "offsetDistance" : 25 * mm});
        }
        {
            var Q0;
            Q0=makeQuery(id+"F1.opExtrude","SWEPT_FACE",FACE,{"disambiguationData":[OSD([sQuery(id+"F0.wireOp",EDGE,"E28.MirrorCS")])]});
            cPlane(context, id + "F5", {"entities" : qUnion([Q0]), "cplaneType" : CPlaneType.OFFSET, "offset" : 0 * mm, "width" : 150 * mm, "height" : 150 * mm});
        }
        {
            var Q0;
            Q0=qCreatedBy(id+"F5.planeOp",FACE);
            var sketch = newSketch(context, id + "F6", { "sketchPlane" : qUnion([Q0])});
            skLineSegment(sketch, "E94.0.1", {"start": v(-165, 0) * mm, "end": v(-165, 6) * mm});
            skLineSegment(sketch, "E94.0.2", {"start": v(-165, 6) * mm, "end": v(-195, 6) * mm});
            skLineSegment(sketch, "E94.0.3", {"start": v(-195, 6) * mm, "end": v(-195, 0) * mm});
            skLineSegment(sketch, "E95.0.1", {"start": v(15, 0) * mm, "end": v(15, 6) * mm});
            skLineSegment(sketch, "E95.0.2", {"start": v(15, 6) * mm, "end": v(-15, 6) * mm});
            skLineSegment(sketch, "E95.0.3", {"start": v(-15, 6) * mm, "end": v(-15, 0) * mm});
            skLineSegment(sketch, "E96.0.1", {"start": v(195, 0) * mm, "end": v(195, 6) * mm});
            skLineSegment(sketch, "E96.0.2", {"start": v(195, 6) * mm, "end": v(165, 6) * mm});
            skLineSegment(sketch, "E96.0.3", {"start": v(165, 6) * mm, "end": v(165, 0) * mm});
            skLineSegment(sketch, "E97.0.1", {"start": v(-195, -90) * mm, "end": v(-195, -96) * mm});
            skLineSegment(sketch, "E97.0.2", {"start": v(-195, -96) * mm, "end": v(-165, -96) * mm});
            skLineSegment(sketch, "E97.0.3", {"start": v(-165, -96) * mm, "end": v(-165, -90) * mm});
            skLineSegment(sketch, "E98.0.1", {"start": v(-15, -90) * mm, "end": v(-15, -96) * mm});
            skLineSegment(sketch, "E98.0.2", {"start": v(-15, -96) * mm, "end": v(15, -96) * mm});
            skLineSegment(sketch, "E98.0.3", {"start": v(15, -96) * mm, "end": v(15, -90) * mm});
            skLineSegment(sketch, "E99.0.1", {"start": v(165, -90) * mm, "end": v(165, -96) * mm});
            skLineSegment(sketch, "E99.0.2", {"start": v(165, -96) * mm, "end": v(195, -96) * mm});
            skLineSegment(sketch, "E99.0.3", {"start": v(195, -96) * mm, "end": v(195, -90) * mm});
            skPoint(sketch, "E100.0", {"position": v(-207.9, 6) * mm});
            skPoint(sketch, "E101.0", {"position": v(-207.9, -90) * mm});
            skPoint(sketch, "E102.0", {"position": v(207.9, -90) * mm});
            skPoint(sketch, "E103.0", {"position": v(207.9, 6) * mm});
            skLineSegment(sketch, "E104", {"start": v(-165, 0) * mm, "end": v(-15, 0) * mm});
            skLineSegment(sketch, "E105", {"start": v(15, 0) * mm, "end": v(165, 0) * mm});
            skLineSegment(sketch, "E106", {"start": v(15, -90) * mm, "end": v(165, -90) * mm});
            skLineSegment(sketch, "E107", {"start": v(-165, -90) * mm, "end": v(-15, -90) * mm});
            skLineSegment(sketch, "E108", {"start": v(-207.9, -45) * mm, "end": v(-207.9, -90) * mm});
            skLineSegment(sketch, "E109", {"start": v(-201.9, -90) * mm, "end": v(-195, -90) * mm});
            skLineSegment(sketch, "E110", {"start": v(-207.9, -45) * mm, "end": v(-201.9, -45) * mm});
            skLineSegment(sketch, "E111", {"start": v(-201.9, -45) * mm, "end": v(-201.9, -90) * mm});
            skLineSegment(sketch, "E112", {"start": v(-207.9, -90) * mm, "end": v(-215.9, -90) * mm});
            skLineSegment(sketch, "E113", {"start": v(-215.9, -90) * mm, "end": v(-215.9, 0) * mm});
            skPoint(sketch, "E114.end.orphan", {"position": v(-207.9, 0) * mm});
            skLineSegment(sketch, "E115", {"start": v(-215.9, 0) * mm, "end": v(-195, 0) * mm});
            skPoint(sketch, "E116.start.orphan", {"position": v(207.9, 0) * mm});
            skLineSegment(sketch, "E117", {"start": v(0, 0) * mm, "end": v(0, -79.06) * mm, "construction": true});
            skLineSegment(sketch, "E118.MirrorCS", {"start": v(215.9, 0) * mm, "end": v(195, 0) * mm});
            skLineSegment(sketch, "E119.MirrorCS", {"start": v(207.9, -45) * mm, "end": v(207.9, -90) * mm});
            skLineSegment(sketch, "E120.MirrorCS", {"start": v(215.9, -90) * mm, "end": v(215.9, 0) * mm});
            skLineSegment(sketch, "E121.MirrorCS", {"start": v(207.9, -90) * mm, "end": v(215.9, -90) * mm});
            skLineSegment(sketch, "E122.MirrorCS", {"start": v(201.9, -45) * mm, "end": v(201.9, -90) * mm});
            skLineSegment(sketch, "E123.MirrorCS", {"start": v(207.9, -45) * mm, "end": v(201.9, -45) * mm});
            skLineSegment(sketch, "E124.MirrorCS", {"start": v(201.9, -90) * mm, "end": v(195, -90) * mm});
            skSolve(sketch);
        }
        {
            var Q0;
            Q0 = qSketchRegion(id + "F6", true);
            extrude(context, id + "F7", {"entities" : qUnion([Q0]), "depth" : 6 * mm, "offsetDistance" : 25 * mm});
        }
        {
            var Q0;
            Q0=makeQuery(id+"F1.opExtrude","SWEPT_FACE",FACE,{"disambiguationData":[OSD([sQuery(id+"F0.wireOp",EDGE,"E34.bottom")])]});
            cPlane(context, id + "F8", {"entities" : qUnion([Q0]), "cplaneType" : CPlaneType.OFFSET, "offset" : 0 * mm, "width" : 150 * mm, "height" : 150 * mm});
        }
        {
            var Q0;
            Q0=qCreatedBy(id+"F8.planeOp",FACE);
            var sketch = newSketch(context, id + "F9", { "sketchPlane" : qUnion([Q0])});
            skLineSegment(sketch, "E125.0.1", {"start": v(-115, 0) * mm, "end": v(-115, 6) * mm});
            skLineSegment(sketch, "E125.0.2", {"start": v(-115, 6) * mm, "end": v(-145, 6) * mm});
            skLineSegment(sketch, "E125.0.3", {"start": v(-145, 6) * mm, "end": v(-145, 0) * mm});
            skLineSegment(sketch, "E126.0.1", {"start": v(15, 0) * mm, "end": v(15, 6) * mm});
            skLineSegment(sketch, "E126.0.2", {"start": v(15, 6) * mm, "end": v(-15, 6) * mm});
            skLineSegment(sketch, "E126.0.3", {"start": v(-15, 6) * mm, "end": v(-15, 0) * mm});
            skLineSegment(sketch, "E127.0.1", {"start": v(145, 0) * mm, "end": v(145, 6) * mm});
            skLineSegment(sketch, "E127.0.2", {"start": v(145, 6) * mm, "end": v(115, 6) * mm});
            skLineSegment(sketch, "E127.0.3", {"start": v(115, 6) * mm, "end": v(115, 0) * mm});
            skLineSegment(sketch, "E128.0.1", {"start": v(115, -90) * mm, "end": v(115, -96) * mm});
            skLineSegment(sketch, "E128.0.2", {"start": v(115, -96) * mm, "end": v(145, -96) * mm});
            skLineSegment(sketch, "E128.0.3", {"start": v(145, -96) * mm, "end": v(145, -90) * mm});
            skLineSegment(sketch, "E129.0.1", {"start": v(-15, -90) * mm, "end": v(-15, -96) * mm});
            skLineSegment(sketch, "E129.0.2", {"start": v(-15, -96) * mm, "end": v(15, -96) * mm});
            skLineSegment(sketch, "E129.0.3", {"start": v(15, -96) * mm, "end": v(15, -90) * mm});
            skLineSegment(sketch, "E130.0.1", {"start": v(-145, -90) * mm, "end": v(-145, -96) * mm});
            skLineSegment(sketch, "E130.0.2", {"start": v(-145, -96) * mm, "end": v(-115, -96) * mm});
            skLineSegment(sketch, "E130.0.3", {"start": v(-115, -96) * mm, "end": v(-115, -90) * mm});
            skPoint(sketch, "E131.0", {"position": v(-157.9, -96) * mm});
            skPoint(sketch, "E132.0", {"position": v(-157.9, 0) * mm});
            skPoint(sketch, "E133.0", {"position": v(158.1, 0) * mm});
            skLineSegment(sketch, "E134.0.1", {"start": v(152.1, -45) * mm, "end": v(158.1, -45) * mm});
            skLineSegment(sketch, "E135.MirrorCS", {"start": v(158.1, -45) * mm, "end": v(158.1, 0) * mm});
            skLineSegment(sketch, "E136.MirrorCS", {"start": v(152.1, 0) * mm, "end": v(152.1, -45) * mm});
            skPoint(sketch, "E134.0.3.end.orphan", {"position": v(152.1, -90) * mm});
            skPoint(sketch, "E134.0.3.start.orphan", {"position": v(158.1, -90) * mm});
            skLineSegment(sketch, "E137", {"start": v(152.1, 0) * mm, "end": v(145, 0) * mm});
            skLineSegment(sketch, "E138", {"start": v(115, 0) * mm, "end": v(15, 0) * mm});
            skLineSegment(sketch, "E139", {"start": v(-15, 0) * mm, "end": v(-115, 0) * mm});
            skLineSegment(sketch, "E140", {"start": v(-115, -90) * mm, "end": v(-15, -90) * mm});
            skLineSegment(sketch, "E141", {"start": v(15, -90) * mm, "end": v(115, -90) * mm});
            skLineSegment(sketch, "E142", {"start": v(158.1, 0) * mm, "end": v(166.1, 0) * mm});
            skLineSegment(sketch, "E143", {"start": v(166.1, 0) * mm, "end": v(166.1, -90) * mm});
            skLineSegment(sketch, "E144", {"start": v(166.1, -90) * mm, "end": v(145, -90) * mm});
            skLineSegment(sketch, "E145", {"start": v(0, 0) * mm, "end": v(0, -52.76) * mm, "construction": true});
            skLineSegment(sketch, "E146.MirrorCS", {"start": v(-152.1, 0) * mm, "end": v(-145, 0) * mm});
            skLineSegment(sketch, "E147.MirrorCS", {"start": v(-152.1, -45) * mm, "end": v(-158.1, -45) * mm});
            skLineSegment(sketch, "E148.MirrorCS", {"start": v(-158.1, 0) * mm, "end": v(-166.1, 0) * mm});
            skLineSegment(sketch, "E149.MirrorCS", {"start": v(-166.1, -90) * mm, "end": v(-145, -90) * mm});
            skPoint(sketch, "E150.MirrorP", {"position": v(-158.1, 0) * mm});
            skPoint(sketch, "E151.MirrorP", {"position": v(-158.1, -90) * mm});
            skLineSegment(sketch, "E152.MirrorCS", {"start": v(-158.1, -45) * mm, "end": v(-158.1, 0) * mm});
            skLineSegment(sketch, "E153.MirrorCS", {"start": v(-152.1, 0) * mm, "end": v(-152.1, -45) * mm});
            skLineSegment(sketch, "E154.MirrorCS", {"start": v(-166.1, 0) * mm, "end": v(-166.1, -90) * mm});
            skPoint(sketch, "E155.MirrorP", {"position": v(-152.1, -90) * mm});
            skSolve(sketch);
        }
        {
            var Q0;
            Q0 = qSketchRegion(id + "F9", true);
            extrude(context, id + "F10", {"entities" : qUnion([Q0]), "depth" : 6 * mm, "offsetDistance" : 25 * mm});
        }
        {
            var Q0;
            Q0=makeQuery(id+"F10.opExtrude","SWEPT_BODY",BODY,{"disambiguationData":[OSD([sQuery(id+"F9.wireOp",EDGE,"E125.0.1"),sQuery(id+"F9.wireOp",EDGE,"E125.0.2"),sQuery(id+"F9.wireOp",EDGE,"E125.0.3"),sQuery(id+"F9.wireOp",EDGE,"E126.0.1"),sQuery(id+"F9.wireOp",EDGE,"E126.0.2"),sQuery(id+"F9.wireOp",EDGE,"E126.0.3"),sQuery(id+"F9.wireOp",EDGE,"E127.0.1"),sQuery(id+"F9.wireOp",EDGE,"E127.0.2"),sQuery(id+"F9.wireOp",EDGE,"E127.0.3"),sQuery(id+"F9.wireOp",EDGE,"E128.0.1"),sQuery(id+"F9.wireOp",EDGE,"E128.0.2"),sQuery(id+"F9.wireOp",EDGE,"E128.0.3"),sQuery(id+"F9.wireOp",EDGE,"E129.0.1"),sQuery(id+"F9.wireOp",EDGE,"E129.0.2"),sQuery(id+"F9.wireOp",EDGE,"E129.0.3"),sQuery(id+"F9.wireOp",EDGE,"E130.0.1"),sQuery(id+"F9.wireOp",EDGE,"E130.0.2"),sQuery(id+"F9.wireOp",EDGE,"E130.0.3"),sQuery(id+"F9.wireOp",EDGE,"E134.0.1"),sQuery(id+"F9.wireOp",EDGE,"E135.MirrorCS"),sQuery(id+"F9.wireOp",EDGE,"E136.MirrorCS"),sQuery(id+"F9.wireOp",EDGE,"E137"),sQuery(id+"F9.wireOp",EDGE,"E138"),sQuery(id+"F9.wireOp",EDGE,"E139"),sQuery(id+"F9.wireOp",EDGE,"E140"),sQuery(id+"F9.wireOp",EDGE,"E141"),sQuery(id+"F9.wireOp",EDGE,"E142"),sQuery(id+"F9.wireOp",EDGE,"E143"),sQuery(id+"F9.wireOp",EDGE,"E144"),sQuery(id+"F9.wireOp",EDGE,"E146.MirrorCS"),sQuery(id+"F9.wireOp",EDGE,"E147.MirrorCS"),sQuery(id+"F9.wireOp",EDGE,"E148.MirrorCS"),sQuery(id+"F9.wireOp",EDGE,"E149.MirrorCS"),sQuery(id+"F9.wireOp",EDGE,"E152.MirrorCS"),sQuery(id+"F9.wireOp",EDGE,"E153.MirrorCS"),sQuery(id+"F9.wireOp",EDGE,"E154.MirrorCS")])]});
            var Q1;
            Q1=qCreatedBy(makeId("Right.planeOp"),FACE);
            mirror(context, id + "F11", {"entities" : qUnion([Q0]), "mirrorPlane" : qUnion([Q1])});
        }
        {
            var Q0;
            Q0=makeQuery(id+"F7.opExtrude","SWEPT_BODY",BODY,{"disambiguationData":[OSD([sQuery(id+"F6.wireOp",EDGE,"E94.0.1"),sQuery(id+"F6.wireOp",EDGE,"E94.0.2"),sQuery(id+"F6.wireOp",EDGE,"E94.0.3"),sQuery(id+"F6.wireOp",EDGE,"E95.0.1"),sQuery(id+"F6.wireOp",EDGE,"E95.0.2"),sQuery(id+"F6.wireOp",EDGE,"E95.0.3"),sQuery(id+"F6.wireOp",EDGE,"E96.0.1"),sQuery(id+"F6.wireOp",EDGE,"E96.0.2"),sQuery(id+"F6.wireOp",EDGE,"E96.0.3"),sQuery(id+"F6.wireOp",EDGE,"E97.0.1"),sQuery(id+"F6.wireOp",EDGE,"E97.0.2"),sQuery(id+"F6.wireOp",EDGE,"E97.0.3"),sQuery(id+"F6.wireOp",EDGE,"E98.0.1"),sQuery(id+"F6.wireOp",EDGE,"E98.0.2"),sQuery(id+"F6.wireOp",EDGE,"E98.0.3"),sQuery(id+"F6.wireOp",EDGE,"E99.0.1"),sQuery(id+"F6.wireOp",EDGE,"E99.0.2"),sQuery(id+"F6.wireOp",EDGE,"E99.0.3"),sQuery(id+"F6.wireOp",EDGE,"E104"),sQuery(id+"F6.wireOp",EDGE,"E105"),sQuery(id+"F6.wireOp",EDGE,"E106"),sQuery(id+"F6.wireOp",EDGE,"E107"),sQuery(id+"F6.wireOp",EDGE,"E108"),sQuery(id+"F6.wireOp",EDGE,"E109"),sQuery(id+"F6.wireOp",EDGE,"E110"),sQuery(id+"F6.wireOp",EDGE,"E111"),sQuery(id+"F6.wireOp",EDGE,"E112"),sQuery(id+"F6.wireOp",EDGE,"E113"),sQuery(id+"F6.wireOp",EDGE,"E115"),sQuery(id+"F6.wireOp",EDGE,"E118.MirrorCS"),sQuery(id+"F6.wireOp",EDGE,"E119.MirrorCS"),sQuery(id+"F6.wireOp",EDGE,"E120.MirrorCS"),sQuery(id+"F6.wireOp",EDGE,"E121.MirrorCS"),sQuery(id+"F6.wireOp",EDGE,"E122.MirrorCS"),sQuery(id+"F6.wireOp",EDGE,"E123.MirrorCS"),sQuery(id+"F6.wireOp",EDGE,"E124.MirrorCS")])]});
            var Q1;
            Q1=qCreatedBy(makeId("Front.planeOp"),FACE);
            mirror(context, id + "F12", {"entities" : qUnion([Q0]), "mirrorPlane" : qUnion([Q1])});
        }
        {
            var Q0;
            Q0=qCreatedBy(makeId("Front.planeOp"),FACE);
            var sketch = newSketch(context, id + "F13", { "sketchPlane" : qUnion([Q0])});
            skLineSegment(sketch, "E156.bottom", {"start": v(-30, 0) * mm, "end": v(30, 0) * mm});
            skLineSegment(sketch, "E156.top", {"start": v(-30, -90) * mm, "end": v(-3, -90) * mm});
            skLineSegment(sketch, "E156.left", {"start": v(-30, 0) * mm, "end": v(-30, -90) * mm});
            skLineSegment(sketch, "E156.right", {"start": v(30, 0) * mm, "end": v(30, -90) * mm});
            skLineSegment(sketch, "E157", {"start": v(-3, -45) * mm, "end": v(3, -45) * mm});
            skPoint(sketch, "E157.startSnap0", {"position": v(-30, -45) * mm});
            skLineSegment(sketch, "E158", {"start": v(3, -45) * mm, "end": v(3, -90) * mm});
            skLineSegment(sketch, "E159", {"start": v(-3, -45) * mm, "end": v(-3, -90) * mm});
            skLineSegment(sketch, "E160.trimOffspring", {"start": v(3, -90) * mm, "end": v(30, -90) * mm});
            skSolve(sketch);
        }
        {
            var Q0;
            Q0 = qSketchRegion(id + "F13", true);
            extrude(context, id + "F14", {"entities" : qUnion([Q0]), "endBound" : BoundingType.SYMMETRIC, "depth" : 6 * mm, "offsetDistance" : 25 * mm});
        }
        {
            var Q0;
            Q0=qCreatedBy(makeId("Right.planeOp"),FACE);
            var sketch = newSketch(context, id + "F15", { "sketchPlane" : qUnion([Q0])});
            skLineSegment(sketch, "E161.bottom", {"start": v(-30.96, 0) * mm, "end": v(-3.96, 0) * mm});
            skLineSegment(sketch, "E161.left", {"start": v(-30.96, 0) * mm, "end": v(-30.96, -90) * mm});
            skLineSegment(sketch, "E161.right", {"start": v(29.04, 0) * mm, "end": v(29.04, -90) * mm});
            skLineSegment(sketch, "E162", {"start": v(-3.96, -45) * mm, "end": v(2.04, -45) * mm});
            skPoint(sketch, "E162.startSnap0", {"position": v(-30.96, -45) * mm});
            skLineSegment(sketch, "E163.MirrorCS", {"start": v(2.04, -45) * mm, "end": v(2.04, 0) * mm});
            skLineSegment(sketch, "E164.MirrorCS", {"start": v(-3.96, -45) * mm, "end": v(-3.96, 0) * mm});
            skLineSegment(sketch, "E165", {"start": v(-30.96, -90) * mm, "end": v(29.04, -90) * mm});
            skLineSegment(sketch, "E166.trimOffspring", {"start": v(2.04, 0) * mm, "end": v(29.04, 0) * mm});
            skSolve(sketch);
        }
        {
            var Q0;
            Q0 = qSketchRegion(id + "F15", true);
            extrude(context, id + "F16", {"entities" : qUnion([Q0]), "endBound" : BoundingType.SYMMETRIC, "depth" : 6 * mm, "offsetDistance" : 25 * mm});
        }
        {
            var Q0;
            Q0=makeQuery(id+"F1.opExtrude","CAP_FACE",FACE,{"disambiguationData":[OSD([sQuery(id+"F0.wireOp",EDGE,"E0.bottom"),sQuery(id+"F0.wireOp",EDGE,"E0.top"),sQuery(id+"F0.wireOp",EDGE,"E0.left"),sQuery(id+"F0.wireOp",EDGE,"E0.right"),sQuery(id+"F0.wireOp",EDGE,"E1.filletArc"),sQuery(id+"F0.wireOp",EDGE,"E2.filletArc"),sQuery(id+"F0.wireOp",EDGE,"E3.filletArc"),sQuery(id+"F0.wireOp",EDGE,"E4.filletArc"),sQuery(id+"F0.wireOp",EDGE,"E7"),sQuery(id+"F0.wireOp",EDGE,"E8.1.0.0"),sQuery(id+"F0.wireOp",EDGE,"E8.2.0.0"),sQuery(id+"F0.wireOp",EDGE,"E8.3.0.0"),sQuery(id+"F0.wireOp",EDGE,"E8.4.0.0"),sQuery(id+"F0.wireOp",EDGE,"E8.5.0.0"),sQuery(id+"F0.wireOp",EDGE,"E8.6.0.0"),sQuery(id+"F0.wireOp",EDGE,"E8.7.0.0"),sQuery(id+"F0.wireOp",EDGE,"E8.8.0.0"),sQuery(id+"F0.wireOp",EDGE,"E8.9.0.0"),sQuery(id+"F0.wireOp",EDGE,"E8.10.0.0"),sQuery(id+"F0.wireOp",EDGE,"E8.11.0.0"),sQuery(id+"F0.wireOp",EDGE,"E8.12.0.0"),sQuery(id+"F0.wireOp",EDGE,"E8.13.0.0"),sQuery(id+"F0.wireOp",EDGE,"E8.14.0.0"),sQuery(id+"F0.wireOp",EDGE,"E9.1.0.0"),sQuery(id+"F0.wireOp",EDGE,"E9.2.0.0"),sQuery(id+"F0.wireOp",EDGE,"E9.3.0.0"),sQuery(id+"F0.wireOp",EDGE,"E9.4.0.0"),sQuery(id+"F0.wireOp",EDGE,"E9.5.0.0"),sQuery(id+"F0.wireOp",EDGE,"E9.6.0.0"),sQuery(id+"F0.wireOp",EDGE,"E9.7.0.0"),sQuery(id+"F0.wireOp",EDGE,"E9.8.0.0"),sQuery(id+"F0.wireOp",EDGE,"E9.9.0.0"),sQuery(id+"F0.wireOp",EDGE,"E9.10.0.0"),sQuery(id+"F0.wireOp",EDGE,"E9.11.0.0"),sQuery(id+"F0.wireOp",EDGE,"E10.0.15.0"),sQuery(id+"F0.wireOp",EDGE,"E11.1.0.0"),sQuery(id+"F0.wireOp",EDGE,"E11.1.0.1"),sQuery(id+"F0.wireOp",EDGE,"E11.1.0.2"),sQuery(id+"F0.wireOp",EDGE,"E11.1.0.3"),sQuery(id+"F0.wireOp",EDGE,"E11.1.0.4"),sQuery(id+"F0.wireOp",EDGE,"E11.1.0.5"),sQuery(id+"F0.wireOp",EDGE,"E11.1.0.6"),sQuery(id+"F0.wireOp",EDGE,"E11.1.0.7"),sQuery(id+"F0.wireOp",EDGE,"E11.1.0.8"),sQuery(id+"F0.wireOp",EDGE,"E11.1.0.9"),sQuery(id+"F0.wireOp",EDGE,"E11.1.0.10"),sQuery(id+"F0.wireOp",EDGE,"E11.2.0.0"),sQuery(id+"F0.wireOp",EDGE,"E11.2.0.1"),sQuery(id+"F0.wireOp",EDGE,"E11.2.0.2"),sQuery(id+"F0.wireOp",EDGE,"E11.2.0.3"),sQuery(id+"F0.wireOp",EDGE,"E11.2.0.4"),sQuery(id+"F0.wireOp",EDGE,"E11.2.0.5"),sQuery(id+"F0.wireOp",EDGE,"E11.2.0.6"),sQuery(id+"F0.wireOp",EDGE,"E11.2.0.7"),sQuery(id+"F0.wireOp",EDGE,"E11.2.0.8"),sQuery(id+"F0.wireOp",EDGE,"E11.2.0.9"),sQuery(id+"F0.wireOp",EDGE,"E11.2.0.10"),sQuery(id+"F0.wireOp",EDGE,"E11.3.0.0"),sQuery(id+"F0.wireOp",EDGE,"E11.3.0.1"),sQuery(id+"F0.wireOp",EDGE,"E11.3.0.2"),sQuery(id+"F0.wireOp",EDGE,"E11.3.0.3"),sQuery(id+"F0.wireOp",EDGE,"E11.3.0.4"),sQuery(id+"F0.wireOp",EDGE,"E11.3.0.5"),sQuery(id+"F0.wireOp",EDGE,"E11.3.0.6"),sQuery(id+"F0.wireOp",EDGE,"E11.3.0.7"),sQuery(id+"F0.wireOp",EDGE,"E11.3.0.8"),sQuery(id+"F0.wireOp",EDGE,"E11.3.0.9"),sQuery(id+"F0.wireOp",EDGE,"E11.3.0.10"),sQuery(id+"F0.wireOp",EDGE,"E11.4.0.0"),sQuery(id+"F0.wireOp",EDGE,"E11.4.0.1"),sQuery(id+"F0.wireOp",EDGE,"E11.4.0.2"),sQuery(id+"F0.wireOp",EDGE,"E11.4.0.3"),sQuery(id+"F0.wireOp",EDGE,"E11.4.0.4"),sQuery(id+"F0.wireOp",EDGE,"E11.4.0.5"),sQuery(id+"F0.wireOp",EDGE,"E11.4.0.6"),sQuery(id+"F0.wireOp",EDGE,"E11.4.0.7"),sQuery(id+"F0.wireOp",EDGE,"E11.4.0.8"),sQuery(id+"F0.wireOp",EDGE,"E11.4.0.9"),sQuery(id+"F0.wireOp",EDGE,"E11.4.0.10"),sQuery(id+"F0.wireOp",EDGE,"E11.5.0.0"),sQuery(id+"F0.wireOp",EDGE,"E11.5.0.1"),sQuery(id+"F0.wireOp",EDGE,"E11.5.0.2"),sQuery(id+"F0.wireOp",EDGE,"E11.5.0.3"),sQuery(id+"F0.wireOp",EDGE,"E11.5.0.4"),sQuery(id+"F0.wireOp",EDGE,"E11.5.0.5"),sQuery(id+"F0.wireOp",EDGE,"E11.5.0.6"),sQuery(id+"F0.wireOp",EDGE,"E11.5.0.7"),sQuery(id+"F0.wireOp",EDGE,"E11.5.0.8"),sQuery(id+"F0.wireOp",EDGE,"E11.5.0.9"),sQuery(id+"F0.wireOp",EDGE,"E11.5.0.10"),sQuery(id+"F0.wireOp",EDGE,"E11.6.0.0"),sQuery(id+"F0.wireOp",EDGE,"E11.6.0.1"),sQuery(id+"F0.wireOp",EDGE,"E11.6.0.2"),sQuery(id+"F0.wireOp",EDGE,"E11.6.0.3"),sQuery(id+"F0.wireOp",EDGE,"E11.6.0.4"),sQuery(id+"F0.wireOp",EDGE,"E11.6.0.5"),sQuery(id+"F0.wireOp",EDGE,"E11.6.0.6"),sQuery(id+"F0.wireOp",EDGE,"E11.6.0.7"),sQuery(id+"F0.wireOp",EDGE,"E11.6.0.8"),sQuery(id+"F0.wireOp",EDGE,"E11.6.0.9"),sQuery(id+"F0.wireOp",EDGE,"E11.6.0.10"),sQuery(id+"F0.wireOp",EDGE,"E11.7.0.0"),sQuery(id+"F0.wireOp",EDGE,"E11.7.0.1"),sQuery(id+"F0.wireOp",EDGE,"E11.7.0.2"),sQuery(id+"F0.wireOp",EDGE,"E11.7.0.3"),sQuery(id+"F0.wireOp",EDGE,"E11.7.0.4"),sQuery(id+"F0.wireOp",EDGE,"E11.7.0.5"),sQuery(id+"F0.wireOp",EDGE,"E11.7.0.6"),sQuery(id+"F0.wireOp",EDGE,"E11.7.0.7"),sQuery(id+"F0.wireOp",EDGE,"E11.7.0.8"),sQuery(id+"F0.wireOp",EDGE,"E11.7.0.9"),sQuery(id+"F0.wireOp",EDGE,"E11.7.0.10"),sQuery(id+"F0.wireOp",EDGE,"E11.8.0.0"),sQuery(id+"F0.wireOp",EDGE,"E11.8.0.1"),sQuery(id+"F0.wireOp",EDGE,"E11.8.0.2"),sQuery(id+"F0.wireOp",EDGE,"E11.8.0.3"),sQuery(id+"F0.wireOp",EDGE,"E11.8.0.4"),sQuery(id+"F0.wireOp",EDGE,"E11.8.0.5"),sQuery(id+"F0.wireOp",EDGE,"E11.8.0.6"),sQuery(id+"F0.wireOp",EDGE,"E11.8.0.7"),sQuery(id+"F0.wireOp",EDGE,"E11.8.0.8"),sQuery(id+"F0.wireOp",EDGE,"E11.8.0.9"),sQuery(id+"F0.wireOp",EDGE,"E11.8.0.10"),sQuery(id+"F0.wireOp",EDGE,"E11.9.0.0"),sQuery(id+"F0.wireOp",EDGE,"E11.9.0.1"),sQuery(id+"F0.wireOp",EDGE,"E11.9.0.2"),sQuery(id+"F0.wireOp",EDGE,"E11.9.0.3"),sQuery(id+"F0.wireOp",EDGE,"E11.9.0.4"),sQuery(id+"F0.wireOp",EDGE,"E11.9.0.5"),sQuery(id+"F0.wireOp",EDGE,"E11.9.0.6"),sQuery(id+"F0.wireOp",EDGE,"E11.9.0.7"),sQuery(id+"F0.wireOp",EDGE,"E11.9.0.8"),sQuery(id+"F0.wireOp",EDGE,"E11.9.0.9"),sQuery(id+"F0.wireOp",EDGE,"E11.9.0.10"),sQuery(id+"F0.wireOp",EDGE,"E11.10.0.0"),sQuery(id+"F0.wireOp",EDGE,"E11.10.0.1"),sQuery(id+"F0.wireOp",EDGE,"E11.10.0.2"),sQuery(id+"F0.wireOp",EDGE,"E11.10.0.3"),sQuery(id+"F0.wireOp",EDGE,"E11.10.0.4"),sQuery(id+"F0.wireOp",EDGE,"E11.10.0.5"),sQuery(id+"F0.wireOp",EDGE,"E11.10.0.6"),sQuery(id+"F0.wireOp",EDGE,"E11.10.0.7"),sQuery(id+"F0.wireOp",EDGE,"E11.10.0.8"),sQuery(id+"F0.wireOp",EDGE,"E11.10.0.9"),sQuery(id+"F0.wireOp",EDGE,"E11.10.0.10"),sQuery(id+"F0.wireOp",EDGE,"E11.11.0.0"),sQuery(id+"F0.wireOp",EDGE,"E11.11.0.1"),sQuery(id+"F0.wireOp",EDGE,"E11.11.0.2"),sQuery(id+"F0.wireOp",EDGE,"E11.11.0.3"),sQuery(id+"F0.wireOp",EDGE,"E11.11.0.4"),sQuery(id+"F0.wireOp",EDGE,"E11.11.0.5"),sQuery(id+"F0.wireOp",EDGE,"E11.11.0.6"),sQuery(id+"F0.wireOp",EDGE,"E11.11.0.7"),sQuery(id+"F0.wireOp",EDGE,"E11.11.0.8"),sQuery(id+"F0.wireOp",EDGE,"E11.11.0.9"),sQuery(id+"F0.wireOp",EDGE,"E11.11.0.10"),sQuery(id+"F0.wireOp",EDGE,"E11.12.0.0"),sQuery(id+"F0.wireOp",EDGE,"E11.12.0.1"),sQuery(id+"F0.wireOp",EDGE,"E11.12.0.2"),sQuery(id+"F0.wireOp",EDGE,"E11.12.0.3"),sQuery(id+"F0.wireOp",EDGE,"E11.12.0.4"),sQuery(id+"F0.wireOp",EDGE,"E11.12.0.5"),sQuery(id+"F0.wireOp",EDGE,"E11.12.0.6"),sQuery(id+"F0.wireOp",EDGE,"E11.12.0.7"),sQuery(id+"F0.wireOp",EDGE,"E11.12.0.8"),sQuery(id+"F0.wireOp",EDGE,"E11.12.0.9"),sQuery(id+"F0.wireOp",EDGE,"E11.12.0.10"),sQuery(id+"F0.wireOp",EDGE,"E11.13.0.0"),sQuery(id+"F0.wireOp",EDGE,"E11.13.0.1"),sQuery(id+"F0.wireOp",EDGE,"E11.13.0.2"),sQuery(id+"F0.wireOp",EDGE,"E11.13.0.3"),sQuery(id+"F0.wireOp",EDGE,"E11.13.0.4"),sQuery(id+"F0.wireOp",EDGE,"E11.13.0.5"),sQuery(id+"F0.wireOp",EDGE,"E11.13.0.6"),sQuery(id+"F0.wireOp",EDGE,"E11.13.0.7"),sQuery(id+"F0.wireOp",EDGE,"E11.13.0.8"),sQuery(id+"F0.wireOp",EDGE,"E11.13.0.9"),sQuery(id+"F0.wireOp",EDGE,"E11.13.0.10"),sQuery(id+"F0.wireOp",EDGE,"E11.14.0.0"),sQuery(id+"F0.wireOp",EDGE,"E11.14.0.1"),sQuery(id+"F0.wireOp",EDGE,"E11.14.0.2"),sQuery(id+"F0.wireOp",EDGE,"E11.14.0.3"),sQuery(id+"F0.wireOp",EDGE,"E11.14.0.4"),sQuery(id+"F0.wireOp",EDGE,"E11.14.0.5"),sQuery(id+"F0.wireOp",EDGE,"E11.14.0.6"),sQuery(id+"F0.wireOp",EDGE,"E11.14.0.7"),sQuery(id+"F0.wireOp",EDGE,"E11.14.0.8"),sQuery(id+"F0.wireOp",EDGE,"E11.14.0.9"),sQuery(id+"F0.wireOp",EDGE,"E11.14.0.10"),sQuery(id+"F0.wireOp",EDGE,"E11.15.0.0"),sQuery(id+"F0.wireOp",EDGE,"E11.15.0.1"),sQuery(id+"F0.wireOp",EDGE,"E11.15.0.2"),sQuery(id+"F0.wireOp",EDGE,"E11.15.0.3"),sQuery(id+"F0.wireOp",EDGE,"E11.15.0.4"),sQuery(id+"F0.wireOp",EDGE,"E11.15.0.5"),sQuery(id+"F0.wireOp",EDGE,"E11.15.0.6"),sQuery(id+"F0.wireOp",EDGE,"E11.15.0.7"),sQuery(id+"F0.wireOp",EDGE,"E11.15.0.8"),sQuery(id+"F0.wireOp",EDGE,"E11.15.0.9"),sQuery(id+"F0.wireOp",EDGE,"E11.15.0.10"),sQuery(id+"F0.wireOp",EDGE,"E15.bottom"),sQuery(id+"F0.wireOp",EDGE,"E15.top"),sQuery(id+"F0.wireOp",EDGE,"E15.left"),sQuery(id+"F0.wireOp",EDGE,"E15.right"),sQuery(id+"F0.wireOp",EDGE,"E16.bottom"),sQuery(id+"F0.wireOp",EDGE,"E16.top"),sQuery(id+"F0.wireOp",EDGE,"E16.left"),sQuery(id+"F0.wireOp",EDGE,"E16.right"),sQuery(id+"F0.wireOp",EDGE,"E17.MirrorCS"),sQuery(id+"F0.wireOp",EDGE,"E18.MirrorCS"),sQuery(id+"F0.wireOp",EDGE,"E19.MirrorCS"),sQuery(id+"F0.wireOp",EDGE,"E20.MirrorCS"),sQuery(id+"F0.wireOp",EDGE,"E21.MirrorCS"),sQuery(id+"F0.wireOp",EDGE,"E22.MirrorCS"),sQuery(id+"F0.wireOp",EDGE,"E23.MirrorCS"),sQuery(id+"F0.wireOp",EDGE,"E24.MirrorCS"),sQuery(id+"F0.wireOp",EDGE,"E25.MirrorCS"),sQuery(id+"F0.wireOp",EDGE,"E26.MirrorCS"),sQuery(id+"F0.wireOp",EDGE,"E27.MirrorCS"),sQuery(id+"F0.wireOp",EDGE,"E28.MirrorCS"),sQuery(id+"F0.wireOp",EDGE,"E29.MirrorCS"),sQuery(id+"F0.wireOp",EDGE,"E30.MirrorCS"),sQuery(id+"F0.wireOp",EDGE,"E31.MirrorCS"),sQuery(id+"F0.wireOp",EDGE,"E32.MirrorCS"),sQuery(id+"F0.wireOp",EDGE,"E33.bottom"),sQuery(id+"F0.wireOp",EDGE,"E33.top"),sQuery(id+"F0.wireOp",EDGE,"E33.right"),sQuery(id+"F0.wireOp",EDGE,"E34.bottom"),sQuery(id+"F0.wireOp",EDGE,"E34.top"),sQuery(id+"F0.wireOp",EDGE,"E34.left"),sQuery(id+"F0.wireOp",EDGE,"E34.right"),sQuery(id+"F0.wireOp",EDGE,"E35.MirrorCS"),sQuery(id+"F0.wireOp",EDGE,"E36.MirrorCS"),sQuery(id+"F0.wireOp",EDGE,"E37.MirrorCS"),sQuery(id+"F0.wireOp",EDGE,"E38.MirrorCS"),sQuery(id+"F0.wireOp",EDGE,"E33.left"),sQuery(id+"F0.wireOp",EDGE,"E39.MirrorCS"),sQuery(id+"F0.wireOp",EDGE,"E40.MirrorCS"),sQuery(id+"F0.wireOp",EDGE,"E41.MirrorCS"),sQuery(id+"F0.wireOp",EDGE,"E42.MirrorCS"),sQuery(id+"F0.wireOp",EDGE,"E43.MirrorCS"),sQuery(id+"F0.wireOp",EDGE,"E44.MirrorCS"),sQuery(id+"F0.wireOp",EDGE,"E45.MirrorCS"),sQuery(id+"F0.wireOp",EDGE,"E46.MirrorCS"),sQuery(id+"F0.wireOp",EDGE,"E47.MirrorCS"),sQuery(id+"F0.wireOp",EDGE,"E48.MirrorCS"),sQuery(id+"F0.wireOp",EDGE,"E49.MirrorCS"),sQuery(id+"F0.wireOp",EDGE,"E50.MirrorCS")])],"isStart":false});
            cPlane(context, id + "F17", {"entities" : qUnion([Q0]), "cplaneType" : CPlaneType.OFFSET, "offset" : 50 * mm, "width" : 150 * mm, "height" : 150 * mm});
        }
        {
            var Q0;
            Q0=qCreatedBy(id+"F17.planeOp",FACE);
            var sketch = newSketch(context, id + "F18", { "sketchPlane" : qUnion([Q0])});
            skLineSegment(sketch, "E167.0", {"start": v(205, 175) * mm, "end": v(-205, 175) * mm});
            skArc(sketch, "E168.0", {"start": v(-205, 175) * mm, "mid": v(-219.14, 169.14) * mm, "end": v(-225, 155) * mm});
            skLineSegment(sketch, "E169.0", {"start": v(-225, 155) * mm, "end": v(-225, -155) * mm});
            skPoint(sketch, "E170.0", {"position": v(219.14, 169.14) * mm});
            skLineSegment(sketch, "E171.0", {"start": v(225, 155) * mm, "end": v(225, -155) * mm});
            skArc(sketch, "E172.0", {"start": v(-225, -155) * mm, "mid": v(-219.14, -169.14) * mm, "end": v(-205, -175) * mm});
            skLineSegment(sketch, "E173.0", {"start": v(205, -175) * mm, "end": v(-205, -175) * mm});
            skArc(sketch, "E174.0", {"start": v(205, -175) * mm, "mid": v(219.14, -169.14) * mm, "end": v(225, -155) * mm});
            skArc(sketch, "E175.0", {"start": v(225, 155) * mm, "mid": v(219.14, 169.14) * mm, "end": v(205, 175) * mm});
            skLineSegment(sketch, "E176", {"start": v(-195, 145) * mm, "end": v(-195, -145) * mm});
            skLineSegment(sketch, "E177", {"start": v(-195, 145) * mm, "end": v(195, 145) * mm});
            skLineSegment(sketch, "E178.MirrorCS", {"start": v(195, 145) * mm, "end": v(195, -145) * mm});
            skLineSegment(sketch, "E179.MirrorCS", {"start": v(-195, -145) * mm, "end": v(195, -145) * mm});
            skPoint(sketch, "E180.orphan", {"position": v(197.28, 145) * mm});
            skPoint(sketch, "E181.start.orphan", {"position": v(0, 145) * mm});
            skSolve(sketch);
        }
        {
            var Q0;
            Q0 = qSketchRegion(id + "F18", true);
            extrude(context, id + "F19", {"entities" : qUnion([Q0]), "depth" : 6 * mm, "offsetDistance" : 25 * mm});
        }
        {
            var Q0;
            Q0=makeQuery(id+"F19.opExtrude","SWEPT_BODY",BODY,{"disambiguationData":[OSD([sQuery(id+"F18.wireOp",EDGE,"E167.0"),sQuery(id+"F18.wireOp",EDGE,"E168.0"),sQuery(id+"F18.wireOp",EDGE,"E169.0"),sQuery(id+"F18.wireOp",EDGE,"E171.0"),sQuery(id+"F18.wireOp",EDGE,"E172.0"),sQuery(id+"F18.wireOp",EDGE,"E173.0"),sQuery(id+"F18.wireOp",EDGE,"E174.0"),sQuery(id+"F18.wireOp",EDGE,"E175.0"),sQuery(id+"F18.wireOp",EDGE,"E176"),sQuery(id+"F18.wireOp",EDGE,"E177"),sQuery(id+"F18.wireOp",EDGE,"E178.MirrorCS"),sQuery(id+"F18.wireOp",EDGE,"E179.MirrorCS")])]});
            var Q1;
            Q1=makeQuery(id+"F19.opExtrude","CAP_FACE",FACE,{"disambiguationData":[OSD([sQuery(id+"F18.wireOp",EDGE,"E167.0"),sQuery(id+"F18.wireOp",EDGE,"E168.0"),sQuery(id+"F18.wireOp",EDGE,"E169.0"),sQuery(id+"F18.wireOp",EDGE,"E171.0"),sQuery(id+"F18.wireOp",EDGE,"E172.0"),sQuery(id+"F18.wireOp",EDGE,"E173.0"),sQuery(id+"F18.wireOp",EDGE,"E174.0"),sQuery(id+"F18.wireOp",EDGE,"E175.0"),sQuery(id+"F18.wireOp",EDGE,"E176"),sQuery(id+"F18.wireOp",EDGE,"E177"),sQuery(id+"F18.wireOp",EDGE,"E178.MirrorCS"),sQuery(id+"F18.wireOp",EDGE,"E179.MirrorCS")])],"isStart":false});
            mirror(context, id + "F20", {"entities" : qUnion([Q0]), "mirrorPlane" : qUnion([Q1])});
        }
        {
            var Q0;
            Q0=makeQuery(id+"F20.opPattern","COPY",BODY,{"derivedFrom":makeQuery(id+"F19.opExtrude","SWEPT_BODY",BODY,{"disambiguationData":[OSD([sQuery(id+"F18.wireOp",EDGE,"E167.0"),sQuery(id+"F18.wireOp",EDGE,"E168.0"),sQuery(id+"F18.wireOp",EDGE,"E169.0"),sQuery(id+"F18.wireOp",EDGE,"E171.0"),sQuery(id+"F18.wireOp",EDGE,"E172.0"),sQuery(id+"F18.wireOp",EDGE,"E173.0"),sQuery(id+"F18.wireOp",EDGE,"E174.0"),sQuery(id+"F18.wireOp",EDGE,"E175.0"),sQuery(id+"F18.wireOp",EDGE,"E176"),sQuery(id+"F18.wireOp",EDGE,"E177"),sQuery(id+"F18.wireOp",EDGE,"E178.MirrorCS"),sQuery(id+"F18.wireOp",EDGE,"E179.MirrorCS")])]}),"instanceName":"1"});
            transform(context, id + "F21", {"entities" : qUnion([Q0]), "transformType" : TransformType.TRANSLATION_3D, "dx" : 0 * mm, "dy" : 0 * mm, "dz" : 50 * mm, "makeCopy" : false});
        }
        {
            var Q0;
            Q0=makeQuery(id+"F10.opExtrude","CAP_FACE",FACE,{"disambiguationData":[OSD([sQuery(id+"F9.wireOp",EDGE,"E125.0.1"),sQuery(id+"F9.wireOp",EDGE,"E125.0.2"),sQuery(id+"F9.wireOp",EDGE,"E125.0.3"),sQuery(id+"F9.wireOp",EDGE,"E126.0.1"),sQuery(id+"F9.wireOp",EDGE,"E126.0.2"),sQuery(id+"F9.wireOp",EDGE,"E126.0.3"),sQuery(id+"F9.wireOp",EDGE,"E127.0.1"),sQuery(id+"F9.wireOp",EDGE,"E127.0.2"),sQuery(id+"F9.wireOp",EDGE,"E127.0.3"),sQuery(id+"F9.wireOp",EDGE,"E128.0.1"),sQuery(id+"F9.wireOp",EDGE,"E128.0.2"),sQuery(id+"F9.wireOp",EDGE,"E128.0.3"),sQuery(id+"F9.wireOp",EDGE,"E129.0.1"),sQuery(id+"F9.wireOp",EDGE,"E129.0.2"),sQuery(id+"F9.wireOp",EDGE,"E129.0.3"),sQuery(id+"F9.wireOp",EDGE,"E130.0.1"),sQuery(id+"F9.wireOp",EDGE,"E130.0.2"),sQuery(id+"F9.wireOp",EDGE,"E130.0.3"),sQuery(id+"F9.wireOp",EDGE,"E134.0.1"),sQuery(id+"F9.wireOp",EDGE,"E135.MirrorCS"),sQuery(id+"F9.wireOp",EDGE,"E136.MirrorCS"),sQuery(id+"F9.wireOp",EDGE,"E137"),sQuery(id+"F9.wireOp",EDGE,"E138"),sQuery(id+"F9.wireOp",EDGE,"E139"),sQuery(id+"F9.wireOp",EDGE,"E140"),sQuery(id+"F9.wireOp",EDGE,"E141"),sQuery(id+"F9.wireOp",EDGE,"E142"),sQuery(id+"F9.wireOp",EDGE,"E143"),sQuery(id+"F9.wireOp",EDGE,"E144"),sQuery(id+"F9.wireOp",EDGE,"E146.MirrorCS"),sQuery(id+"F9.wireOp",EDGE,"E147.MirrorCS"),sQuery(id+"F9.wireOp",EDGE,"E148.MirrorCS"),sQuery(id+"F9.wireOp",EDGE,"E149.MirrorCS"),sQuery(id+"F9.wireOp",EDGE,"E152.MirrorCS"),sQuery(id+"F9.wireOp",EDGE,"E153.MirrorCS"),sQuery(id+"F9.wireOp",EDGE,"E154.MirrorCS")])],"isStart":false});
            var sketch = newSketch(context, id + "F22", { "sketchPlane" : qUnion([Q0])});
            skCircle(sketch, "E182", {"center": v(0, -45) * mm, "radius": 20 * mm});
            skLineSegment(sketch, "E183.bottom", {"start": v(-30, -15) * mm, "end": v(30, -15) * mm, "construction": true});
            skLineSegment(sketch, "E183.top", {"start": v(-30, -75) * mm, "end": v(30, -75) * mm, "construction": true});
            skLineSegment(sketch, "E183.left", {"start": v(-30, -15) * mm, "end": v(-30, -75) * mm, "construction": true});
            skLineSegment(sketch, "E183.right", {"start": v(30, -15) * mm, "end": v(30, -75) * mm, "construction": true});
            skLineSegment(sketch, "E184", {"start": v(30, -15) * mm, "end": v(-30, -75) * mm, "construction": true});
            skLineSegment(sketch, "E185", {"start": v(-30, -15) * mm, "end": v(30, -75) * mm, "construction": true});
            skCircle(sketch, "E186", {"center": v(-23.67, -21.33) * mm, "radius": 2 * mm});
            skLineSegment(sketch, "E187", {"start": v(0, -45) * mm, "end": v(0, -32.36) * mm, "construction": true});
            skLineSegment(sketch, "E188", {"start": v(0, -32.36) * mm, "end": v(0, -45) * mm, "construction": true});
            skLineSegment(sketch, "E189", {"start": v(0, -45) * mm, "end": v(12.43, -45) * mm, "construction": true});
            skCircle(sketch, "E190.MirrorC", {"center": v(23.67, -21.33) * mm, "radius": 2 * mm});
            skCircle(sketch, "E191.MirrorC", {"center": v(23.67, -68.67) * mm, "radius": 2 * mm});
            skCircle(sketch, "E192.MirrorC", {"center": v(-23.67, -68.67) * mm, "radius": 2 * mm});
            skSolve(sketch);
        }
        {
            var Q0;
            Q0 = qSketchRegion(id + "F22", true);
            extrude(context, id + "F23", {"entities" : qUnion([Q0]), "operationType" : NewBodyOperationType.REMOVE, "endBound" : BoundingType.SYMMETRIC, "oppositeDirection" : true, "depth" : 25 * mm, "offsetDistance" : 25 * mm});
        }
        {
            var Q0;
            Q0=makeQuery(id+"F10.opExtrude","CAP_FACE",FACE,{"disambiguationData":[OSD([sQuery(id+"F9.wireOp",EDGE,"E125.0.1"),sQuery(id+"F9.wireOp",EDGE,"E125.0.2"),sQuery(id+"F9.wireOp",EDGE,"E125.0.3"),sQuery(id+"F9.wireOp",EDGE,"E126.0.1"),sQuery(id+"F9.wireOp",EDGE,"E126.0.2"),sQuery(id+"F9.wireOp",EDGE,"E126.0.3"),sQuery(id+"F9.wireOp",EDGE,"E127.0.1"),sQuery(id+"F9.wireOp",EDGE,"E127.0.2"),sQuery(id+"F9.wireOp",EDGE,"E127.0.3"),sQuery(id+"F9.wireOp",EDGE,"E128.0.1"),sQuery(id+"F9.wireOp",EDGE,"E128.0.2"),sQuery(id+"F9.wireOp",EDGE,"E128.0.3"),sQuery(id+"F9.wireOp",EDGE,"E129.0.1"),sQuery(id+"F9.wireOp",EDGE,"E129.0.2"),sQuery(id+"F9.wireOp",EDGE,"E129.0.3"),sQuery(id+"F9.wireOp",EDGE,"E130.0.1"),sQuery(id+"F9.wireOp",EDGE,"E130.0.2"),sQuery(id+"F9.wireOp",EDGE,"E130.0.3"),sQuery(id+"F9.wireOp",EDGE,"E134.0.1"),sQuery(id+"F9.wireOp",EDGE,"E135.MirrorCS"),sQuery(id+"F9.wireOp",EDGE,"E136.MirrorCS"),sQuery(id+"F9.wireOp",EDGE,"E137"),sQuery(id+"F9.wireOp",EDGE,"E138"),sQuery(id+"F9.wireOp",EDGE,"E139"),sQuery(id+"F9.wireOp",EDGE,"E140"),sQuery(id+"F9.wireOp",EDGE,"E141"),sQuery(id+"F9.wireOp",EDGE,"E142"),sQuery(id+"F9.wireOp",EDGE,"E143"),sQuery(id+"F9.wireOp",EDGE,"E144"),sQuery(id+"F9.wireOp",EDGE,"E146.MirrorCS"),sQuery(id+"F9.wireOp",EDGE,"E147.MirrorCS"),sQuery(id+"F9.wireOp",EDGE,"E148.MirrorCS"),sQuery(id+"F9.wireOp",EDGE,"E149.MirrorCS"),sQuery(id+"F9.wireOp",EDGE,"E152.MirrorCS"),sQuery(id+"F9.wireOp",EDGE,"E153.MirrorCS"),sQuery(id+"F9.wireOp",EDGE,"E154.MirrorCS")])],"isStart":false});
            cPlane(context, id + "F24", {"entities" : qUnion([Q0]), "cplaneType" : CPlaneType.OFFSET, "offset" : 50 * mm, "width" : 150 * mm, "height" : 150 * mm});
        }
        {
            var Q0;
            Q0=qCreatedBy(id+"F24.planeOp",FACE);
            var sketch = newSketch(context, id + "F25", { "sketchPlane" : qUnion([Q0])});
            skCircle(sketch, "E193.0", {"center": v(0, -45) * mm, "radius": 20 * mm});
            skCircle(sketch, "E194.0", {"center": v(-23.67, -21.33) * mm, "radius": 2 * mm});
            skCircle(sketch, "E195.0", {"center": v(23.67, -21.33) * mm, "radius": 2 * mm});
            skCircle(sketch, "E196.0", {"center": v(-23.67, -68.67) * mm, "radius": 2 * mm});
            skCircle(sketch, "E197.0", {"center": v(23.67, -68.67) * mm, "radius": 2 * mm});
            skLineSegment(sketch, "E198.bottom", {"start": v(-25, -15) * mm, "end": v(25, -15) * mm});
            skLineSegment(sketch, "E198.top", {"start": v(-25, -75) * mm, "end": v(25, -75) * mm});
            skLineSegment(sketch, "E198.left", {"start": v(-30, -20) * mm, "end": v(-30, -70) * mm});
            skLineSegment(sketch, "E198.right", {"start": v(30, -20) * mm, "end": v(30, -70) * mm});
            skPoint(sketch, "E199.visualSharp", {"position": v(-30, -15) * mm});
            skArc(sketch, "E199.filletArc", {"start": v(-25, -15) * mm, "mid": v(-28.54, -16.46) * mm, "end": v(-30, -20) * mm});
            skPoint(sketch, "E200.visualSharp", {"position": v(30, -15) * mm});
            skArc(sketch, "E200.filletArc", {"start": v(30, -20) * mm, "mid": v(28.54, -16.46) * mm, "end": v(25, -15) * mm});
            skPoint(sketch, "E201.visualSharp", {"position": v(30, -75) * mm});
            skArc(sketch, "E201.filletArc", {"start": v(25, -75) * mm, "mid": v(28.54, -73.54) * mm, "end": v(30, -70) * mm});
            skPoint(sketch, "E202.visualSharp", {"position": v(-30, -75) * mm});
            skArc(sketch, "E202.filletArc", {"start": v(-30, -70) * mm, "mid": v(-28.54, -73.54) * mm, "end": v(-25, -75) * mm});
            skCircle(sketch, "E203", {"center": v(0, -45) * mm, "radius": 17.5 * mm});
            skSolve(sketch);
        }
        {
            var Q0;
            Q0=makeQuery(id+"F25.imprint","IMPRINT",FACE,{"disambiguationData":[TD([[makeQuery(id+"F25.imprint","IMPRINT",EDGE,{"derivedFrom":sQuery(id+"F25.wireOp",EDGE,"E193.0")}),1.0]])]});
            var Q1;
            Q1=sQuery(id+"F25.wireOp",EDGE,"E193.0");
            extrude(context, id + "F26", {"entities" : qUnion([Q0]), "surfaceEntities" : qUnion([Q1]), "depth" : 40 * mm, "offsetDistance" : 25 * mm});
        }
        {
            var Q0;
            Q0=makeQuery(id+"F25.imprint","IMPRINT",FACE,{"disambiguationData":[TD([[makeQuery(id+"F25.imprint","IMPRINT",EDGE,{"derivedFrom":sQuery(id+"F25.wireOp",EDGE,"E193.0")}),-1.0]])]});
            extrude(context, id + "F27", {"entities" : qUnion([Q0]), "operationType" : NewBodyOperationType.ADD, "depth" : 6 * mm, "offsetDistance" : 25 * mm});
        }
    });
